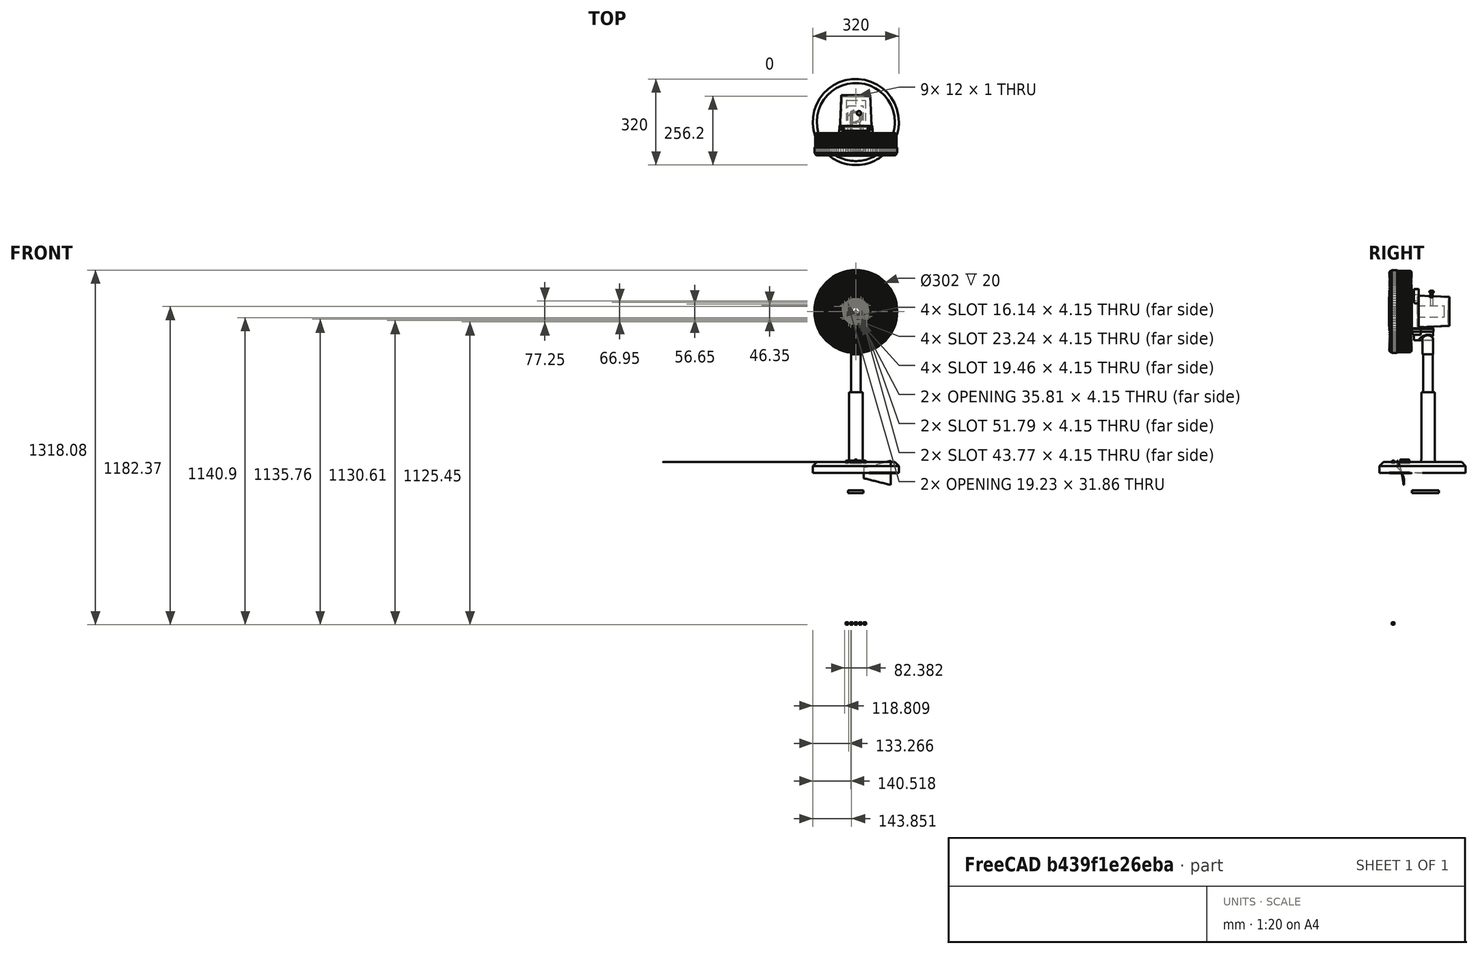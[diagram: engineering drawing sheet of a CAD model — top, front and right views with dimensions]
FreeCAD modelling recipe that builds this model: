
FCSTD DOCUMENT  (FreeCAD 1.0R39109 (Git))
Label: fan
License: All rights reserved
LicenseURL: https://en.wikipedia.org/wiki/All_rights_reserved
objects: Sketcher::SketchObject×53, PartDesign::Pad×37, Part::FeaturePython×22, PartDesign::ShapeBinder×20, PartDesign::Fillet×19, PartDesign::Plane×15, PartDesign::Body×13, App::Part×11, PartDesign::Pocket×9, PartDesign::Line×6, Part::Extrusion×4, PartDesign::Boolean×4, PartDesign::Chamfer×2, Surface::GeomFillSurface×1, Part::Part2DObjectPython×1, Part::Sweep×1
note: 394 computed .brp shape members not serialized (recipe doc carries the construction recipe); baked Part::Feature solids carry a one-line shape summary decoded from their .brp

FEATURE [Sketcher::SketchObject] Sketch
  ArcFitTolerance = 1e-06
  AttachmentSupport = -> [XZ_Plane]
  FullyConstrained = true
  MakeInternals = false
  MapMode = 5
  Placement = pos=(0,0,0) rot=(1,0,0;1.5708rad)
  sketch-geometry (2):
    g0: Circle CenterX=0 CenterY=0 CenterZ=0 NormalX=0 NormalY=0 NormalZ=1 AngleXU=0 Radius=25
    g1: Circle CenterX=0 CenterY=0 CenterZ=0 NormalX=0 NormalY=0 NormalZ=1 AngleXU=0 Radius=40
  constraints (4):
    c: Coincident(g0,g-1)
    c: Coincident(g1,g0)
    c: Radius(g0) = 25
    c: Radius(g1) = 40
FEATURE [PartDesign::Pad] Pad
  Direction = (0,-1,2e-16)
  Length = 30
  Length2 = 10
  Midplane = true
  Placement = pos=(0,0,0) rot=(1,0,0;1.5708rad)
  Profile = -> Sketch
  ReferenceAxis = -> Sketch [N_Axis]
  Refine = true
  Suppressed = false
  Type = 0
FEATURE [PartDesign::ShapeBinder] CopyFace
  Placement = pos=(70,0,0) rot=(0,0,1;0rad)
  TraceSupport = false
FEATURE [PartDesign::Plane] DatumPlane
  AttachmentSupport = -> [CopyFace]
  Length = 94.5083
  MapMode = 5
  Placement = pos=(70,0,0) rot=(0.57735,0.57735,0.57735;2.0944rad)
  ResizeMode = 0
  Width = 297.175
FEATURE [PartDesign::ShapeBinder] CopyFace001
  Placement = pos=(170,0,0) rot=(0,0,1;0rad)
  TraceSupport = false
FEATURE [PartDesign::Plane] DatumPlane001
  AttachmentSupport = -> [CopyFace001]
  Length = 94.5083
  MapMode = 5
  Placement = pos=(170,0,0) rot=(0.57735,0.57735,0.57735;2.0944rad)
  ResizeMode = 0
  Width = 297.175
FEATURE [Sketcher::SketchObject] Sketch002
  ArcFitTolerance = 1e-06
  AttachmentSupport = -> [DatumPlane001]
  FullyConstrained = false
  MakeInternals = false
  MapMode = 5
  Placement = pos=(170,0,0) rot=(0.57735,0.57735,0.57735;2.0944rad)
  sketch-geometry (6):
    g0: Circle [constr] CenterX=-11.7502 CenterY=45 CenterZ=0 NormalX=0 NormalY=0 NormalZ=1 AngleXU=0 Radius=1
    g1: Circle [constr] CenterX=4.45153 CenterY=12.5384 CenterZ=0 NormalX=0 NormalY=0 NormalZ=1 AngleXU=0 Radius=1
    g2: Circle [constr] CenterX=11.7502 CenterY=-45 CenterZ=0 NormalX=0 NormalY=0 NormalZ=1 AngleXU=0 Radius=1
    g3: BSplineCurve PolesCount=3 KnotsCount=2 Degree=2 IsPeriodic=0
    g4: GeomPoint [constr] X=-11.7502 Y=45 Z=0
    g5: GeomPoint [constr] X=11.7502 Y=-45 Z=0
  constraints (10):
    c: Weight(g0) = 1
    c: Equal(g0,g1)
    c: Equal(g0,g2)
    c: InternalAlignment(g0,g3)
    c: InternalAlignment(g1,g3)
    c: InternalAlignment(g2,g3)
    c: InternalAlignment(g4,g3)
    c: InternalAlignment(g5,g3)
    c: Symmetric(g3,g3,g-1)
    c: DistanceY(g3) = 45
FEATURE [Sketcher::SketchObject] Sketch001
  ArcFitTolerance = 1e-06
  AttachmentSupport = -> [DatumPlane]
  ExternalGeometry = -> [Sketch002]
  FullyConstrained = false
  MakeInternals = false
  MapMode = 5
  Placement = pos=(70,0,0) rot=(0.57735,0.57735,0.57735;2.0944rad)
  sketch-geometry (6):
    g0: Circle [constr] CenterX=-11.7502 CenterY=20 CenterZ=0 NormalX=0 NormalY=0 NormalZ=1 AngleXU=0 Radius=1
    g1: Circle [constr] CenterX=3.87626 CenterY=6.1367 CenterZ=0 NormalX=0 NormalY=0 NormalZ=1 AngleXU=0 Radius=1
    g2: Circle [constr] CenterX=11.7502 CenterY=-20 CenterZ=0 NormalX=0 NormalY=0 NormalZ=1 AngleXU=0 Radius=1
    g3: BSplineCurve PolesCount=3 KnotsCount=2 Degree=2 IsPeriodic=0
    g4: GeomPoint [constr] X=-11.7502 Y=20 Z=0
    g5: GeomPoint [constr] X=11.7502 Y=-20 Z=0
  constraints (11):
    c: Weight(g0) = 1
    c: Equal(g0,g1)
    c: Equal(g0,g2)
    c: InternalAlignment(g0,g3)
    c: InternalAlignment(g1,g3)
    c: InternalAlignment(g2,g3)
    c: InternalAlignment(g4,g3)
    c: InternalAlignment(g5,g3)
    c: DistanceY(g3,g3) = 40
    c: Symmetric(g3,g3,g-1)
    c: Vertical(g-3,g3)
FEATURE [Surface::GeomFillSurface] Surface
  BoundaryList = -> [Sketch001,Sketch002]
  FillType = 0
FEATURE [Part::Extrusion] Extrude001
  Base = -> Surface
  Dir = (0,1,0)
  DirMode = 0
  FaceMakerClass = Part::FaceMakerBullseye
  FaceMakerMode = 3
  LengthFwd = 1
  LengthRev = 0
  Placement = pos=(-40,0,0) rot=(0,0,1;0rad)
  Solid = true
  Symmetric = false
FEATURE [Sketcher::SketchObject] Sketch003
  ArcFitTolerance = 1e-06
  AttachmentSupport = -> [XZ_Plane]
  FullyConstrained = true
  MakeInternals = false
  MapMode = 5
  Placement = pos=(0,0,0) rot=(1,0,0;1.5708rad)
FEATURE [Sketcher::SketchObject] Sketch004
  ArcFitTolerance = 1e-06
  AttachmentSupport = -> [XZ_Plane]
  FullyConstrained = false
  MakeInternals = false
  MapMode = 5
  Placement = pos=(0,0,0) rot=(1,0,0;1.5708rad)
  sketch-geometry (6):
    g0: LineSegment StartX=-63.2233 StartY=0.5 StartZ=0 EndX=-63.2233 EndY=-0.5 EndZ=0
    g1: LineSegment StartX=-63.2233 StartY=-0.5 StartZ=0 EndX=-21.9541 EndY=-0.5 EndZ=0
    g2: LineSegment StartX=-21.9541 StartY=-0.5 StartZ=0 EndX=-21.9541 EndY=0.5 EndZ=0
    g3: LineSegment StartX=-21.9541 StartY=0.5 StartZ=0 EndX=-63.2233 EndY=0.5 EndZ=0
    g4: GeomPoint [constr] X=-42.5887 Y=1e-16 Z=0
    g5: Circle CenterX=0 CenterY=0 CenterZ=0 NormalX=0 NormalY=0 NormalZ=1 AngleXU=0 Radius=40
  constraints (12):
    c: Coincident(g0,g1)
    c: Coincident(g1,g2)
    c: Coincident(g2,g3)
    c: Coincident(g3,g0)
    c: Vertical(g0)
    c: Horizontal(g1)
    c: Horizontal(g3)
    c: Symmetric(g2,g0,g4)
    c: DistanceY(g2,g2) = 1
    c: Symmetric(g2,g1,g-1)
    c: Diameter(g5) = 80
    c: Coincident(g5,g-1)
FEATURE [Part::FeaturePython] Array  # Draft array (typed FeaturePython)
  AlwaysSyncPlacement = false
  Angle = 360
  ArrayType = 1
  Axis = (0,1,0)
  Base = -> Extrude001
  Center = (0,0,0)
  Count = 6
  ExpandArray = false
  Fuse = false
  IntervalAxis = (0,0,0)
  IntervalX = (50,0,0)
  IntervalY = (0,50,0)
  IntervalZ = (0,0,50)
  NumberCircles = 3
  NumberPolar = 6
  NumberX = 2
  NumberY = 2
  NumberZ = 1
  PlacementList = 6 placements: [(-40,0,0),(-20,0,34.641),(20,0,34.641),(40,0,4.89859e-15),(20,0,-34.641),(-20,0,-34.641)]
  RadialDistance = 50
  ScaleList = (6) [(1,1,1),(1,1,1),(1,1,1),(1,1,1),(1,1,1),(1,1,1)]
  Symmetry = 1
  TangentialDistance = 25
FEATURE [PartDesign::Boolean] Boolean
  BaseFeature = -> Pad
  Group = -> [Array]
  Refine = true
  Suppressed = false
  Type = 0
  UsePlacement = true
FEATURE [Sketcher::SketchObject] Sketch005
  ArcFitTolerance = 1e-06
  AttachmentSupport = -> [XZ_Plane]
  FullyConstrained = false
  MakeInternals = false
  MapMode = 5
  Placement = pos=(0,0,0) rot=(1,0,0;1.5708rad)
  sketch-geometry (6):
    g0: LineSegment StartX=5.87739 StartY=0.5 StartZ=0 EndX=5.87739 EndY=-0.5 EndZ=0
    g1: LineSegment StartX=5.87739 StartY=-0.5 StartZ=0 EndX=25.7123 EndY=-0.5 EndZ=0
    g2: LineSegment StartX=25.7123 StartY=-0.5 StartZ=0 EndX=25.7123 EndY=0.5 EndZ=0
    g3: LineSegment StartX=25.7123 StartY=0.5 StartZ=0 EndX=5.87739 EndY=0.5 EndZ=0
    g4: GeomPoint [constr] X=15.7948 Y=1e-16 Z=0
    g5: Circle [constr] CenterX=0 CenterY=0 CenterZ=0 NormalX=0 NormalY=0 NormalZ=1 AngleXU=0 Radius=15
  constraints (12):
    c: Coincident(g0,g1)
    c: Coincident(g1,g2)
    c: Coincident(g2,g3)
    c: Coincident(g3,g0)
    c: Vertical(g2)
    c: Horizontal(g1)
    c: Horizontal(g3)
    c: Symmetric(g2,g0,g4)
    c: Diameter(g5) = 30
    c: Coincident(g5,g-1)
    c: Symmetric(g0,g0,g-1)
    c: DistanceY(g0,g0) = 1
FEATURE [Part::Extrusion] Extrude
  Base = -> Sketch005
  Dir = (0,-1,2e-16)
  DirMode = 2
  FaceMakerClass = Part::FaceMakerBullseye
  FaceMakerMode = 3
  LengthFwd = 25
  LengthRev = 0
  Solid = true
  Symmetric = true
FEATURE [Part::FeaturePython] Array001  # Draft array (typed FeaturePython)
  AlwaysSyncPlacement = false
  Angle = 360
  ArrayType = 1
  Axis = (0,1,0)
  Base = -> Extrude
  Center = (0,0,0)
  Count = 6
  ExpandArray = false
  Fuse = false
  IntervalAxis = (0,0,0)
  IntervalX = (50,0,0)
  IntervalY = (0,50,0)
  IntervalZ = (0,0,50)
  NumberCircles = 3
  NumberPolar = 6
  NumberX = 2
  NumberY = 2
  NumberZ = 1
  PlacementList = 6 placements: [(0,0,0),(0,0,0),(0,0,0),(0,0,0),(0,0,0),(0,0,0)]
  RadialDistance = 50
  ScaleList = (6) [(1,1,1),(1,1,1),(1,1,1),(1,1,1),(1,1,1),(1,1,1)]
  Symmetry = 1
  TangentialDistance = 25
FEATURE [PartDesign::Boolean] Boolean001
  BaseFeature = -> Boolean
  Group = -> [Array001]
  Refine = true
  Suppressed = false
  Type = 0
  UsePlacement = true
FEATURE [Sketcher::SketchObject] Sketch006
  ArcFitTolerance = 1e-06
  AttachmentSupport = -> [XZ_Plane]
  FullyConstrained = true
  MakeInternals = false
  MapMode = 5
  Placement = pos=(0,0,0) rot=(1,0,0;1.5708rad)
  sketch-geometry (1):
    g0: Circle CenterX=0 CenterY=0 CenterZ=0 NormalX=0 NormalY=0 NormalZ=1 AngleXU=0 Radius=15
  constraints (2):
    c: Diameter(g0) = 30
    c: Coincident(g0,g-1)
FEATURE [PartDesign::Pad] Pad001
  BaseFeature = -> Boolean001
  Direction = (0,-1,2e-16)
  Length = 30
  Length2 = 10
  Midplane = true
  Profile = -> Sketch006
  ReferenceAxis = -> Sketch006 [N_Axis]
  Refine = true
  Suppressed = false
  Type = 0
FEATURE [Sketcher::SketchObject] Sketch007
  ArcFitTolerance = 1e-06
  AttachmentSupport = -> [Pad001]
  FullyConstrained = true
  MakeInternals = false
  MapMode = 5
  Placement = pos=(0,-12.5,0) rot=(1,0,0;1.5708rad)
  sketch-geometry (1):
    g0: Circle CenterX=0 CenterY=0 CenterZ=0 NormalX=0 NormalY=0 NormalZ=1 AngleXU=0 Radius=25
  constraints (2):
    c: Coincident(g0,g-1)
    c: Radius(g0) = 25
FEATURE [PartDesign::Pad] Pad002
  BaseFeature = -> Pad001
  Direction = (0,-1,2e-16)
  Length = 5
  Length2 = 10
  Profile = -> Sketch007
  ReferenceAxis = -> Sketch007 [N_Axis]
  Refine = true
  Reversed = true
  Suppressed = false
  Type = 0
FEATURE [PartDesign::Chamfer] Chamfer
  Angle = 45
  Base = -> Pad002 [Edge116]
  BaseFeature = -> Pad002
  ChamferType = 0
  FlipDirection = false
  Refine = true
  Size = 2.3
  Size2 = 1
  SupportTransform = false
  Suppressed = false
  UseAllEdges = false
FEATURE [Sketcher::SketchObject] Sketch008
  ArcFitTolerance = 1e-06
  AttachmentSupport = -> [Chamfer]
  FullyConstrained = true
  MakeInternals = false
  MapMode = 5
  Placement = pos=(0,-12.5,2.9e-15) rot=(1,0,0;1.5708rad)
  sketch-geometry (1):
    g0: Circle CenterX=0 CenterY=0 CenterZ=0 NormalX=0 NormalY=0 NormalZ=1 AngleXU=0 Radius=17.5
  constraints (2):
    c: Diameter(g0) = 35
    c: Coincident(g0,g-1)
FEATURE [PartDesign::Pad] Pad003
  BaseFeature = -> Chamfer
  Direction = (0,-1,2e-16)
  Length = 10
  Length2 = 10
  Profile = -> Sketch008
  ReferenceAxis = -> Sketch008 [N_Axis]
  Refine = true
  Suppressed = false
  Type = 0
FEATURE [PartDesign::Plane] DatumPlane002
  AttachmentOffset = pos=(0,0,20) rot=(0,0,1;0rad)
  AttachmentSupport = -> [Pad003]
  Length = 313.007
  MapMode = 5
  Placement = pos=(0,-42.5,9.6e-15) rot=(1,0,0;1.5708rad)
  ResizeMode = 0
  Width = 323.174
FEATURE [PartDesign::Plane] CopyDatumPlane002
  Length = 362.396
  Placement = pos=(0,-42.5,9.7e-15) rot=(1,0,0;1.5708rad)
  ResizeMode = 0
  Width = 362.396
FEATURE [Sketcher::SketchObject] Sketch009
  ArcFitTolerance = 1e-06
  AttachmentSupport = -> [CopyDatumPlane002]
  FullyConstrained = true
  MakeInternals = false
  MapMode = 5
  Placement = pos=(0,-42.5,9.7e-15) rot=(1,0,0;1.5708rad)
  sketch-geometry (1):
    g0: Circle CenterX=0 CenterY=0 CenterZ=0 NormalX=0 NormalY=0 NormalZ=1 AngleXU=0 Radius=55
  constraints (2):
    c: Diameter(g0) = 110
    c: Coincident(g0,g-1)
FEATURE [PartDesign::Pad] Pad004
  Direction = (0,-1,2e-16)
  Length = 5
  Length2 = 10
  Placement = pos=(0,-42.5,9.7e-15) rot=(1,0,0;1.5708rad)
  Profile = -> Sketch009
  ReferenceAxis = -> Sketch009 [N_Axis]
  Refine = true
  Reversed = true
  Suppressed = false
  Type = 0
FEATURE [Sketcher::SketchObject] Sketch011
  ArcFitTolerance = 1e-06
  FullyConstrained = false
  MakeInternals = false
  Placement = pos=(0,0,9.1e-15) rot=(0,0,1;0rad)
  sketch-geometry (5):
    g0: LineSegment StartX=145 StartY=40 StartZ=0 EndX=50 EndY=40 EndZ=0
    g1: LineSegment StartX=145 StartY=-40 StartZ=0 EndX=50 EndY=-40 EndZ=0
    g2: LineSegment StartX=150 StartY=-35 StartZ=0 EndX=150 EndY=35 EndZ=0
    g3: ArcOfCircle CenterX=145 CenterY=35 CenterZ=0 NormalX=0 NormalY=0 NormalZ=1 AngleXU=0 Radius=5 StartAngle=3e-16 EndAngle=1.5708
    g4: ArcOfCircle CenterX=145 CenterY=-35 CenterZ=0 NormalX=0 NormalY=0 NormalZ=1 AngleXU=0 Radius=5 StartAngle=4.71239 EndAngle=6.28319
  constraints (13):
    c: Horizontal(g0)
    c: Horizontal(g1)
    c: Vertical(g2)
    c: Tangent(g0,g3) = -1.5708
    c: Tangent(g2,g3) = -1.5708
    c: Tangent(g2,g4) = -1.5708
    c: Tangent(g1,g4) = 1.5708
    c: DistanceY(g1,g0) = 80
    c: DistanceY(g0) = 40
    c: DistanceX(g1) = 50
    c: DistanceX(g2) = 150
    c: Equal(g3,g4)
    c: Radius(g4) = 5
FEATURE [Part::Part2DObjectPython] Circle  # Draft 2D object (typed FeaturePython)
  Area = 3.14159
  FirstAngle = 0
  LastAngle = 0
  MakeFace = true
  Placement = pos=(50,-40,9.1e-15) rot=(0.57735,0.57735,0.57735;2.0944rad)
  Radius = 1
FEATURE [Part::Sweep] Sweep
  Frenet = true
  Sections = -> [Circle]
  Solid = true
  Spine = -> Sketch011 [Edge1,Edge2,Edge3,Edge4,Edge5]
  Transition = 1
FEATURE [Sketcher::SketchObject] Sketch012
  ArcFitTolerance = 1e-06
  AttachmentSupport = -> [Pad003]
  FullyConstrained = true
  MakeInternals = false
  MapMode = 5
  Placement = pos=(0,15,0) rot=(0,0.707107,0.707107;3.14159rad)
  sketch-geometry (1):
    g0: Circle CenterX=0 CenterY=0 CenterZ=0 NormalX=0 NormalY=0 NormalZ=1 AngleXU=0 Radius=2.5
  constraints (2):
    c: Diameter(g0) = 5
    c: Coincident(g0,g-1)
FEATURE [PartDesign::ShapeBinder] CopyPad005
  Placement = pos=(0,25,-5.6e-15) rot=(0,0,1;0rad)
  TraceSupport = false
FEATURE [Sketcher::SketchObject] Sketch013
  ArcFitTolerance = 1e-06
  AttachmentSupport = -> [CopyPad005]
  FullyConstrained = false
  MakeInternals = false
  MapMode = 5
  Placement = pos=(0,40,-5.6e-15) rot=(0,0.707107,0.707107;3.14159rad)
  sketch-geometry (30):
    g0: ArcOfCircle CenterX=0 CenterY=0 CenterZ=0 NormalX=0 NormalY=0 NormalZ=1 AngleXU=0 Radius=55 StartAngle=6.28319 EndAngle=7.85398
    g1: ArcOfCircle CenterX=0 CenterY=0 CenterZ=0 NormalX=0 NormalY=0 NormalZ=1 AngleXU=0 Radius=49.6 StartAngle=0.107844 EndAngle=0.711077
    g2: ArcOfCircle CenterX=0 CenterY=0 CenterZ=0 NormalX=0 NormalY=0 NormalZ=1 AngleXU=0 Radius=25 StartAngle=2.8576e-06 EndAngle=1.5708
    g3: LineSegment StartX=3.85478 StartY=44.0604 StartZ=0 EndX=4.23487 EndY=48.4048 EndZ=0
    g4: ArcOfCircle CenterX=0 CenterY=0 CenterZ=0 NormalX=0 NormalY=0 NormalZ=1 AngleXU=0 Radius=49.6 StartAngle=0.912359 EndAngle=1.46295
    g5: ArcOfCircle CenterX=0 CenterY=0 CenterZ=0 NormalX=0 NormalY=0 NormalZ=1 AngleXU=0 Radius=43.24 StartAngle=0.917739 EndAngle=1.46092
    g6: ArcOfCircle CenterX=0 CenterY=0 CenterZ=0 NormalX=0 NormalY=0 NormalZ=1 AngleXU=0 Radius=43.24 StartAngle=0.109872 EndAngle=0.691605
    g7: ArcOfCircle CenterX=0 CenterY=0 CenterZ=0 NormalX=0 NormalY=0 NormalZ=1 AngleXU=0 Radius=37.84 StartAngle=0.114414 EndAngle=1.45638
    g8: ArcOfCircle CenterX=0 CenterY=0 CenterZ=0 NormalX=0 NormalY=0 NormalZ=1 AngleXU=0 Radius=31.49 StartAngle=0.11805 EndAngle=1.45275
    g9: LineSegment StartX=27.6374 StartY=34.4826 StartZ=0 EndX=30.4939 EndY=37.786 EndZ=0
    g10: LineSegment StartX=3.20963 StartY=36.6863 StartZ=0 EndX=2.83035 EndY=32.351 EndZ=0
    g11: LineSegment StartX=32.351 StartY=2.83035 StartZ=0 EndX=36.6863 EndY=3.20963 EndZ=0
    g12: LineSegment StartX=33.2878 StartY=28.8322 StartZ=0 EndX=36.0353 EndY=32.3359 EndZ=0
    g13: LineSegment StartX=44.0604 StartY=3.85478 StartZ=0 EndX=48.4048 EndY=4.23487 EndZ=0
    g14: ArcOfCircle CenterX=5.23107 CenterY=48.3177 CenterZ=0 NormalX=0 NormalY=0 NormalZ=1 AngleXU=0 Radius=1 StartAngle=1.46295 EndAngle=3.05433
    g15: ArcOfCircle CenterX=29.7375 CenterY=38.4401 CenterZ=0 NormalX=0 NormalY=0 NormalZ=1 AngleXU=0 Radius=1 StartAngle=5.57022 EndAngle=7.19554
    g16: ArcOfCircle CenterX=36.8222 CenterY=31.7188 CenterZ=0 NormalX=0 NormalY=0 NormalZ=1 AngleXU=0 Radius=1 StartAngle=0.711077 EndAngle=2.47656
    g17: ArcOfCircle CenterX=4.20583 CenterY=36.5991 CenterZ=0 NormalX=0 NormalY=0 NormalZ=1 AngleXU=0 Radius=1 StartAngle=1.45638 EndAngle=3.05433
    g18: ArcOfCircle CenterX=3.82654 CenterY=32.2639 CenterZ=0 NormalX=0 NormalY=0 NormalZ=1 AngleXU=0 Radius=1 StartAngle=3.05433 EndAngle=4.59434
    g19: ArcOfCircle CenterX=4.85098 CenterY=43.9732 CenterZ=0 NormalX=0 NormalY=0 NormalZ=1 AngleXU=0 Radius=1 StartAngle=3.05433 EndAngle=4.60252
    g20: ArcOfCircle CenterX=32.2639 CenterY=3.82654 CenterZ=0 NormalX=0 NormalY=0 NormalZ=1 AngleXU=0 Radius=1 StartAngle=3.25964 EndAngle=4.79966
    g21: ArcOfCircle CenterX=34.0747 CenterY=28.2151 CenterZ=0 NormalX=0 NormalY=0 NormalZ=1 AngleXU=0 Radius=1 StartAngle=2.47656 EndAngle=3.8332
    g22: ArcOfCircle CenterX=36.5991 CenterY=4.20583 CenterZ=0 NormalX=0 NormalY=0 NormalZ=1 AngleXU=0 Radius=1 StartAngle=4.79964 EndAngle=6.3976
    g23: ArcOfCircle CenterX=43.9732 CenterY=4.85098 CenterZ=0 NormalX=0 NormalY=0 NormalZ=1 AngleXU=0 Radius=1 StartAngle=3.25147 EndAngle=4.79966
    g24: ArcOfCircle CenterX=48.3177 CenterY=5.23107 CenterZ=0 NormalX=0 NormalY=0 NormalZ=1 AngleXU=0 Radius=1 StartAngle=4.79966 EndAngle=6.39103
    g25: ArcOfCircle CenterX=26.881 CenterY=35.1367 CenterZ=0 NormalX=0 NormalY=0 NormalZ=1 AngleXU=0 Radius=1 StartAngle=4.05933 EndAngle=5.57022
    g26: LineSegment StartX=25 StartY=7.144e-05 StartZ=0 EndX=55 EndY=-1.05423e-06 EndZ=0
    g27: LineSegment StartX=-9.21207e-05 StartY=55 StartZ=0 EndX=-9.21207e-05 EndY=25 EndZ=0
    g28: LineSegment [constr] StartX=0 StartY=0 StartZ=0 EndX=76.7679 EndY=6.71632 EndZ=0
    g29: LineSegment [constr] StartX=0 StartY=0 StartZ=0 EndX=4.98246 EndY=56.9498 EndZ=0
  constraints (70):
    c: Diameter(g0) = 110
    c: Diameter(g2) = 50
    c: Tangent(g3,g14) = 1.5708
    c: Tangent(g4,g14) = -1.5708
    c: Tangent(g4,g15) = -1.5708
    c: Tangent(g9,g15) = -1.5708
    c: Tangent(g12,g16) = 1.5708
    c: Tangent(g1,g16) = -1.5708
    c: Tangent(g7,g17) = -1.5708
    c: Tangent(g10,g17) = -1.5708
    c: Tangent(g10,g18) = -1.5708
    c: Tangent(g8,g18) = 1.5708
    c: Tangent(g3,g19) = 1.5708
    c: Tangent(g5,g19) = 1.5708
    c: Tangent(g8,g20) = 1.5708
    c: Tangent(g11,g20) = -1.5708
    c: Tangent(g12,g21) = 1.5708
    c: Tangent(g6,g21) = 1.5708
    c: Tangent(g7,g22) = -1.5708
    c: Tangent(g6,g23) = 1.5708
    c: Tangent(g13,g23) = -1.5708
    c: Tangent(g13,g24) = -1.5708
    c: Tangent(g1,g24) = -1.5708
    c: Tangent(g9,g25) = -1.5708
    c: Tangent(g5,g25) = 1.5708
    c: Coincident(g0,g1)
    c: Coincident(g0,g2)
    c: Coincident(g0,g4)
    c: Coincident(g0,g5)
    c: Coincident(g0,g6)
    c: Coincident(g0,g7)
    c: Coincident(g0,g8)
    c: Coincident(g0,g-1)
    c: Radius(g8) = 31.49
    c: Coincident(g26,g0)
    c: Coincident(g26,g2)
    c: Coincident(g27,g0)
    c: Coincident(g27,g2)
    c: Vertical(g27)
    c: Angle(g-1,g28) = 0.0872665
    c: Coincident(g28,g0)
    c: Tangent(g28,g22)
    c: Coincident(g29,g0)
    c: Angle(g29,g-2) = 0.0872665
    c: Radius(g7) = 37.84
    c: Radius(g6) = 43.24
    c: Radius(g1) = 49.6
    c: Radius(g5) = 43.24
    c: Radius(g4) = 49.6
    c: PointOnObject(g10,g29)
    c: PointOnObject(g10,g29)
    c: PointOnObject(g3,g29)
    c: PointOnObject(g3,g29)
    c: PointOnObject(g13,g28)
    c: PointOnObject(g13,g28)
    c: PointOnObject(g11,g28)
    c: PointOnObject(g11,g28)
    c: Equal(g17,g18)
    c: Equal(g17,g20)
    c: Equal(g17,g22)
    c: Equal(g17,g23)
    c: Equal(g17,g24)
    c: Equal(g17,g16)
    c: Equal(g17,g21)
    c: Equal(g17,g15)
    c: Equal(g17,g25)
    c: Equal(g17,g14)
    c: Equal(g17,g19)
    c: Radius(g17) = 1
    c: Coincident(g22,g11)
FEATURE [PartDesign::Pad] Pad006
  Direction = (0,1,-2e-16)
  Length = 5
  Length2 = 10
  Midplane = true
  Placement = pos=(0,25,-5.6e-15) rot=(0,0,1;0rad)
  Profile = -> Sketch013
  ReferenceAxis = -> Sketch013 [N_Axis]
  Refine = true
  Suppressed = false
  Type = 0
FEATURE [Sketcher::SketchObject] Sketch014
  ArcFitTolerance = 1e-06
  AttachmentSupport = -> [Pad006]
  FullyConstrained = false
  MakeInternals = false
  MapMode = 5
  Placement = pos=(0,37.5,-5.6e-15) rot=(1,0,0;1.5708rad)
  sketch-geometry (23):
    g0: Circle CenterX=-1.805e-13 CenterY=-1.057e-13 CenterZ=0 NormalX=0 NormalY=0 NormalZ=1 AngleXU=0 Radius=15
    g1: ArcOfCircle CenterX=-1.805e-13 CenterY=-1.057e-13 CenterZ=0 NormalX=0 NormalY=0 NormalZ=1 AngleXU=0 Radius=35 StartAngle=2.53435 EndAngle=2.70164
    g2: ArcOfCircle CenterX=35.3365 CenterY=61.2046 CenterZ=0 NormalX=0 NormalY=0 NormalZ=1 AngleXU=0 Radius=41.7572 StartAngle=3.82376 EndAngle=4.55382
    g3: ArcOfCircle CenterX=70.673 CenterY=-7.1e-15 CenterZ=0 NormalX=0 NormalY=0 NormalZ=1 AngleXU=0 Radius=41.7572 StartAngle=2.77656 EndAngle=3.50662
    g4: ArcOfCircle CenterX=35.3365 CenterY=-61.2046 CenterZ=0 NormalX=0 NormalY=0 NormalZ=1 AngleXU=0 Radius=41.7572 StartAngle=1.72937 EndAngle=2.45943
    g5: ArcOfCircle CenterX=-35.3365 CenterY=-61.2046 CenterZ=0 NormalX=0 NormalY=0 NormalZ=1 AngleXU=0 Radius=41.7572 StartAngle=0.682168 EndAngle=1.41223
    g6: ArcOfCircle CenterX=-70.673 CenterY=-7.1e-15 CenterZ=0 NormalX=0 NormalY=0 NormalZ=1 AngleXU=0 Radius=41.7572 StartAngle=5.91816 EndAngle=6.64822
    g7: ArcOfCircle CenterX=-35.3365 CenterY=61.2046 CenterZ=0 NormalX=0 NormalY=0 NormalZ=1 AngleXU=0 Radius=41.7572 StartAngle=4.87096 EndAngle=5.60102
    g8: LineSegment [constr] StartX=-31.667 StartY=14.9064 StartZ=0 EndX=-31.667 EndY=-14.9064 EndZ=0
    g9: LineSegment [constr] StartX=31.667 StartY=14.9064 StartZ=0 EndX=31.667 EndY=-14.9064 EndZ=0
    g10: LineSegment [constr] StartX=-35.3365 StartY=61.2046 StartZ=0 EndX=-1.776e-13 EndY=-1.066e-13 EndZ=0
    g11: LineSegment [constr] StartX=35.3365 StartY=61.2046 StartZ=0 EndX=-1.776e-13 EndY=-1.066e-13 EndZ=0
    g12: ArcOfCircle CenterX=-1.805e-13 CenterY=-1.057e-13 CenterZ=0 NormalX=0 NormalY=0 NormalZ=1 AngleXU=0 Radius=35 StartAngle=3.58155 EndAngle=3.74884
    g13: ArcOfCircle CenterX=-1.805e-13 CenterY=-1.057e-13 CenterZ=0 NormalX=0 NormalY=0 NormalZ=1 AngleXU=0 Radius=35 StartAngle=4.62874 EndAngle=4.79604
    g14: ArcOfCircle CenterX=-1.805e-13 CenterY=-1.057e-13 CenterZ=0 NormalX=0 NormalY=0 NormalZ=1 AngleXU=0 Radius=35 StartAngle=5.67594 EndAngle=5.84323
    g15: ArcOfCircle CenterX=-1.805e-13 CenterY=-1.057e-13 CenterZ=0 NormalX=0 NormalY=0 NormalZ=1 AngleXU=0 Radius=35 StartAngle=0.439952 EndAngle=0.607245
    g16: ArcOfCircle CenterX=-1.805e-13 CenterY=-1.057e-13 CenterZ=0 NormalX=0 NormalY=0 NormalZ=1 AngleXU=0 Radius=35 StartAngle=1.48715 EndAngle=1.65444
    g17: LineSegment [constr] StartX=-35.3365 StartY=61.2046 StartZ=0 EndX=-70.673 EndY=-7.1e-15 EndZ=0
    g18: LineSegment [constr] StartX=35.3365 StartY=-61.2046 StartZ=0 EndX=70.673 EndY=-7.1e-15 EndZ=0
    g19: LineSegment [constr] StartX=35.3365 StartY=61.2046 StartZ=0 EndX=70.673 EndY=-7.1e-15 EndZ=0
    g20: LineSegment [constr] StartX=-35.3365 StartY=-61.2046 StartZ=0 EndX=-70.673 EndY=-7.1e-15 EndZ=0
    g21: LineSegment [constr] StartX=-35.3365 StartY=-61.2046 StartZ=0 EndX=35.3365 EndY=-61.2046 EndZ=0
    g22: LineSegment [constr] StartX=-35.3365 StartY=61.2046 StartZ=0 EndX=35.3365 EndY=61.2046 EndZ=0
  constraints (64):
    c: Diameter(g0) = 30
    c: Diameter(g1) = 70
    c: Coincident(g1,g0)
    c: Equal(g7,g2)
    c: Equal(g2,g3)
    c: Equal(g3,g4)
    c: Equal(g4,g5)
    c: Equal(g5,g6)
    c: Symmetric(g3,g6,g-2)
    c: Symmetric(g7,g4,g0)
    c: Symmetric(g2,g5,g0)
    c: Symmetric(g6,g6,g-1)
    c: Coincident(g8,g6)
    c: Coincident(g8,g6)
    c: Coincident(g9,g3)
    c: Coincident(g9,g3)
    c: Vertical(g9)
    c: Equal(g8,g9)
    c: Coincident(g10,g7)
    c: Coincident(g10,g0)
    c: Angle(g-1,g10) = 2.0944
    c: Coincident(g11,g2)
    c: Coincident(g11,g0)
    c: Angle(g-1,g11) = 1.0472
    c: PointOnObject(g2,g16)
    c: PointOnObject(g4,g14)
    c: Coincident(g16,g7)
    c: Coincident(g1,g7)
    c: Equal(g1,g12)
    c: Coincident(g1,g6)
    c: PointOnObject(g12,g6)
    c: Coincident(g1,g12)
    c: Equal(g12,g13)
    c: Coincident(g12,g5)
    c: PointOnObject(g13,g5)
    c: Coincident(g12,g13)
    c: Equal(g13,g14)
    c: Coincident(g13,g4)
    c: PointOnObject(g14,g4)
    c: Coincident(g13,g14)
    c: Equal(g14,g15)
    c: PointOnObject(g14,g3)
    c: PointOnObject(g15,g3)
    c: Coincident(g14,g15)
    c: Equal(g15,g16)
    c: PointOnObject(g16,g2)
    c: Coincident(g15,g16)
    c: Coincident(g15,g2)
    c: Symmetric(g5,g4,g-2)
    c: Coincident(g17,g7)
    c: Coincident(g17,g6)
    c: Coincident(g18,g4)
    c: Coincident(g18,g3)
    c: Coincident(g19,g2)
    c: Coincident(g19,g3)
    c: Coincident(g20,g5)
    c: Coincident(g20,g6)
    c: Coincident(g21,g5)
    c: Coincident(g21,g4)
    c: Coincident(g22,g7)
    c: Coincident(g22,g2)
    c: Equal(g19,g21)
    c: Equal(g21,g20)
    c: Equal(g20,g17)
FEATURE [PartDesign::Fillet] Fillet
  Base = -> Pad006 [Edge6,Edge7]
  BaseFeature = -> Pad006
  Placement = pos=(0,25,-5.6e-15) rot=(0,0,1;0rad)
  Radius = 2
  Refine = true
  SupportTransform = false
  Suppressed = false
  UseAllEdges = false
FEATURE [PartDesign::Fillet] Fillet001
  Base = -> Fillet [Edge31,Edge23,Edge49,Edge64,Edge34,Edge57]
  BaseFeature = -> Fillet
  Placement = pos=(0,25,-5.6e-15) rot=(0,0,1;0rad)
  Radius = 1.5
  Refine = true
  SupportTransform = false
  Suppressed = false
  UseAllEdges = false
FEATURE [PartDesign::Pad] Pad007
  BaseFeature = -> Fillet001
  Direction = (0,-1,2e-16)
  Length = 10
  Length2 = 10
  Placement = pos=(0,25,-5.6e-15) rot=(0,0,1;0rad)
  Profile = -> Sketch014
  ReferenceAxis = -> Sketch014 [N_Axis]
  Refine = true
  Suppressed = false
  Type = 0
FEATURE [PartDesign::Fillet] Fillet002
  Base = -> Pad007 [Edge33,Edge108,Edge119,Edge57,Edge126,Edge125,Edge124,Edge123,Edge122,Edge120,Edge105,Edge121]
  BaseFeature = -> Pad007
  Placement = pos=(0,25,-5.6e-15) rot=(0,0,1;0rad)
  Radius = 3
  Refine = true
  SupportTransform = false
  Suppressed = false
  UseAllEdges = false
FEATURE [PartDesign::Fillet] Fillet003
  Base = -> Fillet002 [Edge71]
  BaseFeature = -> Fillet002
  Placement = pos=(0,25,-5.6e-15) rot=(0,0,1;0rad)
  Radius = 4
  Refine = true
  SupportTransform = false
  Suppressed = false
  UseAllEdges = false
FEATURE [Part::FeaturePython] Array002  # Draft array (typed FeaturePython)
  AlwaysSyncPlacement = false
  Angle = 360
  ArrayType = 1
  Axis = (0,1,0)
  Base = -> Fillet001
  Center = (0,0,0)
  Count = 4
  ExpandArray = false
  Fuse = false
  IntervalAxis = (0,0,0)
  IntervalX = (50,0,0)
  IntervalY = (0,50,0)
  IntervalZ = (0,0,50)
  NumberCircles = 3
  NumberPolar = 4
  NumberX = 2
  NumberY = 2
  NumberZ = 1
  PlacementList = 4 placements: [(0,25,-5.6e-15),(-5.6e-15,25,0),(-6.85802e-31,25,5.6e-15),(5.6e-15,25,1.24345e-30)]
  RadialDistance = 50
  ScaleList = (4) [(1,1,1),(1,1,1),(1,1,1),(1,1,1)]
  Symmetry = 1
  TangentialDistance = 25
FEATURE [PartDesign::Boolean] Boolean002
  BaseFeature = -> Fillet003
  Group = -> [Array002]
  Refine = true
  Suppressed = false
  Type = 0
  UsePlacement = true
FEATURE [PartDesign::Body] Body002
  AllowCompound = false
  Group = -> [CopyPad005,Sketch013,Pad006,Sketch014,Fillet,Fillet001,Pad007,Fillet002,Fillet003,Boolean002]
  Origin = -> Origin002
  Tip = -> Boolean002
FEATURE [PartDesign::ShapeBinder] CopyBoolean002
  TraceSupport = false
FEATURE [Sketcher::SketchObject] Sketch015
  ArcFitTolerance = 1e-06
  AttachmentSupport = -> [CopyBoolean002]
  FullyConstrained = true
  MakeInternals = false
  MapMode = 5
  Placement = pos=(0,42.5,0) rot=(0,0.707107,0.707107;3.14159rad)
  sketch-geometry (1):
    g0: Circle CenterX=0 CenterY=0 CenterZ=0 NormalX=0 NormalY=0 NormalZ=1 AngleXU=0 Radius=60
  constraints (2):
    c: Diameter(g0) = 120
    c: Coincident(g0,g-1)
FEATURE [PartDesign::Pad] Pad008
  Direction = (0,1,-2e-16)
  Length = 140
  Length2 = 10
  Profile = -> Sketch015
  ReferenceAxis = -> Sketch015 [N_Axis]
  Refine = true
  Suppressed = false
  TaperAngle = -2.5
  Type = 0
FEATURE [Sketcher::SketchObject] Sketch016
  ArcFitTolerance = 1e-06
  AttachmentSupport = -> [Pad008]
  FullyConstrained = true
  MakeInternals = false
  MapMode = 5
  Placement = pos=(0,42.5,-9.4e-15) rot=(1,0,0;1.5708rad)
  sketch-geometry (1):
    g0: Circle CenterX=0 CenterY=0 CenterZ=0 NormalX=0 NormalY=0 NormalZ=1 AngleXU=0 Radius=62.5
  constraints (2):
    c: Diameter(g0) = 125
    c: Coincident(g0,g-1)
FEATURE [PartDesign::Pad] Pad009
  BaseFeature = -> Pad008
  Direction = (0,-1,2e-16)
  Length = 25
  Length2 = 10
  Profile = -> Sketch016
  ReferenceAxis = -> Sketch016 [N_Axis]
  Refine = true
  Reversed = true
  Suppressed = false
  TaperAngle = -2.5
  Type = 0
FEATURE [Sketcher::SketchObject] Sketch017
  ArcFitTolerance = 1e-06
  AttachmentSupport = -> [Pad009]
  ExternalGeometry = -> [Pad009]
  FullyConstrained = false
  MakeInternals = false
  MapMode = 5
  Placement = pos=(0,67.5,-1.49e-14) rot=(0,0.707107,0.707107;3.14159rad)
  sketch-geometry (11):
    g0: LineSegment StartX=-54.0278 StartY=29.189 StartZ=0 EndX=-45.1605 EndY=83.7162 EndZ=0
    g1: LineSegment StartX=54.0278 StartY=29.189 StartZ=0 EndX=45.1605 EndY=83.7162 EndZ=0
    g2: LineSegment StartX=45.1605 StartY=83.7162 StartZ=0 EndX=-45.1605 EndY=83.7162 EndZ=0
    g3: LineSegment StartX=-48.063 StartY=38.2223 StartZ=0 EndX=-41.3863 EndY=79.2787 EndZ=0
    g4: LineSegment StartX=-41.3863 StartY=79.2787 StartZ=0 EndX=41.3863 EndY=79.2787 EndZ=0
    g5: LineSegment StartX=41.3863 StartY=79.2787 StartZ=0 EndX=48.063 EndY=38.2223 EndZ=0
    g6: LineSegment [constr] StartX=-43.3631 StartY=67.1232 StartZ=0 EndX=-47.743 EndY=67.8355 EndZ=0
    g7: LineSegment [constr] StartX=-22.8807 StartY=83.7162 StartZ=0 EndX=-22.8807 EndY=79.2787 EndZ=0
    g8: LineSegment [constr] StartX=44.0692 StartY=62.7813 StartZ=0 EndX=48.4491 EndY=63.4935 EndZ=0
    g9: LineSegment StartX=-48.063 StartY=38.2223 StartZ=0 EndX=-54.0278 EndY=29.189 EndZ=0
    g10: LineSegment StartX=48.063 StartY=38.2223 StartZ=0 EndX=54.0278 EndY=29.189 EndZ=0
  constraints (27):
    c: PointOnObject(g0,g-3)
    c: Coincident(g2,g1)
    c: Coincident(g2,g0)
    c: Symmetric(g0,g1,g-2)
    c: Symmetric(g1,g0,g-2)
    c: PointOnObject(g3,g-3)
    c: Coincident(g4,g3)
    c: Horizontal(g4)
    c: Coincident(g5,g4)
    c: PointOnObject(g5,g-3)
    c: Parallel(g3,g0)
    c: Parallel(g5,g1)
    c: PointOnObject(g6,g3)
    c: PointOnObject(g6,g0)
    c: Perpendicular(g3,g6)
    c: PointOnObject(g7,g2)
    c: PointOnObject(g7,g4)
    c: Vertical(g7)
    c: PointOnObject(g8,g5)
    c: PointOnObject(g8,g1)
    c: Perpendicular(g5,g8)
    c: Equal(g8,g7)
    c: Equal(g7,g6)
    c: Coincident(g9,g3)
    c: Coincident(g9,g0)
    c: Coincident(g10,g5)
    c: Coincident(g10,g1)
FEATURE [PartDesign::Pad] Pad010
  BaseFeature = -> Pad009
  Direction = (0,1,-2e-16)
  Length = 17
  Length2 = 10
  Profile = -> Sketch017
  ReferenceAxis = -> Sketch017 [N_Axis]
  Refine = true
  Reversed = true
  Suppressed = false
  Type = 0
FEATURE [Sketcher::SketchObject] Sketch018
  ArcFitTolerance = 1e-06
  AttachmentSupport = -> [Pad010]
  FullyConstrained = true
  MakeInternals = false
  MapMode = 5
  Placement = pos=(0,182.5,-4.02e-14) rot=(0,0.707107,0.707107;3.14159rad)
  sketch-geometry (1):
    g0: Circle CenterX=0 CenterY=0 CenterZ=0 NormalX=0 NormalY=0 NormalZ=1 AngleXU=0 Radius=51
  constraints (2):
    c: Diameter(g0) = 102
    c: Coincident(g0,g-1)
FEATURE [PartDesign::Pocket] Pocket
  BaseFeature = -> Pad010
  Direction = (0,-1,2e-16)
  Length = 120
  Length2 = 5
  Profile = -> Sketch018
  ReferenceAxis = -> Sketch018 [N_Axis]
  Refine = true
  Suppressed = false
  TaperAngle = 2.5
  Type = 0
FEATURE [Sketcher::SketchObject] Sketch019
  ArcFitTolerance = 1e-06
  AttachmentSupport = -> [Pocket]
  FullyConstrained = false
  MakeInternals = false
  MapMode = 5
  Placement = pos=(0,62.5,-1.38e-14) rot=(0,0.707107,0.707107;3.14159rad)
  sketch-geometry (9):
    g0: LineSegment StartX=-23.9794 StartY=-20.7565 StartZ=0 EndX=23.9794 EndY=-20.7565 EndZ=0
    g1: LineSegment StartX=23.9794 StartY=20.7565 StartZ=0 EndX=-23.9794 EndY=20.7565 EndZ=0
    g2: GeomPoint [constr] X=0 Y=0 Z=0
    g3: ArcOfCircle CenterX=-7.77037 CenterY=-8.5e-15 CenterZ=0 NormalX=0 NormalY=0 NormalZ=1 AngleXU=0 Radius=43.5223 StartAngle=5.95653 EndAngle=6.60984
    g4: ArcOfCircle CenterX=7.77037 CenterY=-2.9e-15 CenterZ=0 NormalX=0 NormalY=0 NormalZ=1 AngleXU=0 Radius=43.5223 StartAngle=2.81494 EndAngle=3.46825
    g5: ArcOfCircle CenterX=-23.9794 CenterY=10.7565 CenterZ=0 NormalX=0 NormalY=0 NormalZ=1 AngleXU=0 Radius=10 StartAngle=1.5708 EndAngle=2.81494
    g6: ArcOfCircle CenterX=-23.9794 CenterY=-10.7565 CenterZ=0 NormalX=0 NormalY=0 NormalZ=1 AngleXU=0 Radius=10 StartAngle=3.46825 EndAngle=4.71239
    g7: ArcOfCircle CenterX=23.9794 CenterY=10.7565 CenterZ=0 NormalX=0 NormalY=0 NormalZ=1 AngleXU=0 Radius=10 StartAngle=0.326653 EndAngle=1.5708
    g8: ArcOfCircle CenterX=23.9794 CenterY=-10.7565 CenterZ=0 NormalX=0 NormalY=0 NormalZ=1 AngleXU=0 Radius=10 StartAngle=4.71239 EndAngle=5.95653
  constraints (18):
    c: Horizontal(g0)
    c: Coincident(g2,g-1)
    c: Equal(g4,g3)
    c: Tangent(g4,g5) = -1.5708
    c: Tangent(g1,g5) = -1.5708
    c: Tangent(g4,g6) = -1.5708
    c: Tangent(g0,g6) = -1.5708
    c: Tangent(g1,g7) = -1.5708
    c: Tangent(g3,g7) = -1.5708
    c: Tangent(g0,g8) = -1.5708
    c: Tangent(g3,g8) = -1.5708
    c: Equal(g8,g7)
    c: Equal(g8,g5)
    c: Equal(g8,g6)
    c: Radius(g8) = 10
    c: Symmetric(g7,g6,g2)
    c: Symmetric(g5,g8,g2)
    c: Vertical(g4,g4)
FEATURE [PartDesign::Pad] Pad011
  BaseFeature = -> Pocket
  Direction = (0,1,-2e-16)
  Length = 100
  Length2 = 10
  Profile = -> Sketch019
  ReferenceAxis = -> Sketch019 [N_Axis]
  Refine = true
  Suppressed = false
  Type = 0
FEATURE [Sketcher::SketchObject] Sketch020
  ArcFitTolerance = 1e-06
  AttachmentSupport = -> [Pad011]
  ExternalGeometry = -> [Pad011]
  FullyConstrained = false
  MakeInternals = false
  MapMode = 5
  Placement = pos=(0,42.5,-1.11e-14) rot=(1,0,0;1.5708rad)
  sketch-geometry (2):
    g0: LineSegment [constr] StartX=0 StartY=-62.5 StartZ=0 EndX=0 EndY=-64.5 EndZ=0
    g1: LineSegment StartX=-28.4155 StartY=-64.5 StartZ=0 EndX=28.4155 EndY=-64.5 EndZ=0
  constraints (5):
    c: PointOnObject(g0,g-3)
    c: Vertical(g0)
    c: DistanceY(g0,g0) = 2
    c: Symmetric(g1,g1,g-2)
    c: Symmetric(g1,g1,g0)
FEATURE [Part::Extrusion] Extrude003
  Base = -> Sketch020
  Dir = (0,1,0)
  DirMode = 0
  FaceMakerClass = Part::FaceMakerBullseye
  FaceMakerMode = 3
  LengthFwd = 100
  LengthRev = 0
  Solid = false
  Symmetric = false
FEATURE [PartDesign::ShapeBinder] CopyPad011
  Placement = pos=(0,42.5,-9.4e-15) rot=(1,0,0;1.5708rad)
  TraceSupport = false
FEATURE [PartDesign::Line] DatumLine
  AttacherType = Attacher::AttachEngineLine
  AttachmentSupport = -> [CopyPad011]
  Length = 20
  MapMode = 19
  Placement = pos=(0,42.5,-9.4e-15) rot=(1,0,0;1.5708rad)
  ResizeMode = 0
FEATURE [Part::Extrusion] Extrude004
  Base = -> Extrude003
  Dir = (0,0,-1)
  DirMode = 2
  FaceMakerClass = Part::FaceMakerBullseye
  FaceMakerMode = 3
  LengthFwd = 10
  LengthRev = 0
  Solid = true
  Symmetric = false
FEATURE [PartDesign::ShapeBinder] CopyExtrude003
  TraceSupport = false
FEATURE [PartDesign::Plane] DatumPlane004
  AttachmentSupport = -> [CopyExtrude003]
  Length = 67.1756
  MapMode = 5
  Placement = pos=(0,0,-64.5) rot=(1,0,0;3.14159rad)
  ResizeMode = 0
  Width = 164.676
FEATURE [Sketcher::SketchObject] Sketch021
  ArcFitTolerance = 1e-06
  AttachmentSupport = -> [DatumPlane004]
  ExternalGeometry = -> [CopyPad011]
  FullyConstrained = false
  MakeInternals = false
  MapMode = 5
  Placement = pos=(0,0,-64.5) rot=(1,0,0;3.14159rad)
  sketch-geometry (12):
    g0: GeomPoint [constr] X=0 Y=-146.096 Z=0
    g1: GeomPoint [constr] X=-20 Y=-122.501 Z=0
    g2: GeomPoint [constr] X=20 Y=-122.501 Z=0
    g3: ArcOfCircle CenterX=0.00115096 CenterY=-65.0006 CenterZ=0 NormalX=0 NormalY=0 NormalZ=1 AngleXU=0 Radius=22.5 StartAngle=5.80719 EndAngle=9.90077
    g4: LineSegment StartX=20 StartY=-117.501 StartZ=0 EndX=20 EndY=-75.3107 EndZ=0
    g5: LineSegment StartX=-19.9977 StartY=-75.3106 StartZ=0 EndX=-19.9998 EndY=-117.5 EndZ=0
    g6: LineSegment StartX=-14.9998 StartY=-122.501 StartZ=0 EndX=15 EndY=-122.501 EndZ=0
    g7: GeomPoint [constr] X=0.00115171 Y=-98.9056 Z=0
    g8: ArcOfCircle CenterX=15 CenterY=-117.501 CenterZ=0 NormalX=0 NormalY=0 NormalZ=1 AngleXU=0 Radius=5 StartAngle=4.71239 EndAngle=6.28319
    g9: GeomPoint [constr] X=20 Y=-122.501 Z=0
    g10: ArcOfCircle CenterX=-14.9998 CenterY=-117.501 CenterZ=0 NormalX=0 NormalY=0 NormalZ=1 AngleXU=0 Radius=5 StartAngle=3.14154 EndAngle=4.71239
    g11: GeomPoint [constr] X=-20 Y=-122.501 Z=0
  constraints (15):
    c: DistanceX(g1,g2) = 40
    c: Radius(g3) = 22.5
    c: Symmetric(g5,g9,g7)
    c: Coincident(g4,g3)
    c: PointOnObject(g9,g6)
    c: PointOnObject(g9,g4)
    c: Tangent(g6,g8) = -1.5708
    c: Tangent(g4,g8) = -1.5708
    c: PointOnObject(g11,g6)
    c: PointOnObject(g11,g5)
    c: Tangent(g6,g10) = -1.5708
    c: Tangent(g5,g10) = -1.5708
    c: Equal(g8,g10)
    c: Radius(g8) = 5
    c: Coincident(g3,g5)
FEATURE [PartDesign::Pad] Pad012
  Direction = (0,0,-1)
  Length = 10
  Length2 = 10
  Placement = pos=(0,0,-64.5) rot=(1,0,0;3.14159rad)
  Profile = -> Sketch021
  ReferenceAxis = -> Sketch021 [N_Axis]
  Refine = true
  Suppressed = false
  Type = 0
FEATURE [Sketcher::SketchObject] Sketch022
  ArcFitTolerance = 1e-06
  AttachmentSupport = -> [Pad012]
  ExternalGeometry = -> [Pad012]
  FullyConstrained = false
  MakeInternals = false
  MapMode = 5
  Placement = pos=(0,0,-74.5) rot=(1,0,0;3.14159rad)
  sketch-geometry (12):
    g0: ArcOfCircle CenterX=0.00115096 CenterY=-65.0006 CenterZ=0 NormalX=0 NormalY=0 NormalZ=1 AngleXU=0 Radius=20.5 StartAngle=5.78404 EndAngle=9.92369
    g1: LineSegment StartX=-18 StartY=-74.8092 StartZ=0 EndX=-18 EndY=-117.5 EndZ=0
    g2: LineSegment StartX=-14.9998 StartY=-120.501 StartZ=0 EndX=15 EndY=-120.501 EndZ=0
    g3: LineSegment StartX=18 StartY=-117.501 StartZ=0 EndX=18 EndY=-74.8135 EndZ=0
    g4: LineSegment [constr] StartX=-20 StartY=-122.501 StartZ=0 EndX=-18 EndY=-122.501 EndZ=0
    g5: LineSegment [constr] StartX=-5.54657 StartY=-120.501 StartZ=0 EndX=-5.54657 EndY=-122.501 EndZ=0
    g6: ArcOfCircle CenterX=-14.9998 CenterY=-117.5 CenterZ=0 NormalX=0 NormalY=0 NormalZ=1 AngleXU=0 Radius=3.00024 StartAngle=3.14159 EndAngle=4.71239
    g7: GeomPoint [constr] X=-18 Y=-120.501 Z=0
    g8: ArcOfCircle CenterX=15 CenterY=-117.501 CenterZ=0 NormalX=0 NormalY=0 NormalZ=1 AngleXU=0 Radius=3 StartAngle=4.71239 EndAngle=6.28319
    g9: GeomPoint [constr] X=18 Y=-120.501 Z=0
    g10: LineSegment [constr] StartX=15 StartY=-120.501 StartZ=0 EndX=15 EndY=-122.501 EndZ=0
    g11: LineSegment [constr] StartX=18 StartY=-117.501 StartZ=0 EndX=20 EndY=-117.501 EndZ=0
  constraints (30):
    c: Diameter(g0) = 41
    c: Coincident(g0,g-3)
    c: Vertical(g1)
    c: Vertical(g3)
    c: PointOnObject(g4,g-4)
    c: PointOnObject(g4,g1)
    c: Horizontal(g4)
    c: DistanceX(g4,g4) = 2
    c: Symmetric(g9,g7,g-2)
    c: PointOnObject(g5,g2)
    c: Vertical(g5)
    c: PointOnObject(g5,g-5)
    c: Equal(g5,g4)
    c: PointOnObject(g7,g1)
    c: PointOnObject(g7,g2)
    c: Tangent(g1,g6) = -1.5708
    c: Tangent(g2,g6) = -1.5708
    c: PointOnObject(g9,g3)
    c: PointOnObject(g9,g2)
    c: Tangent(g3,g8) = -1.5708
    c: Tangent(g2,g8) = -1.5708
    c: Coincident(g10,g2)
    c: Coincident(g10,g-5)
    c: Coincident(g11,g3)
    c: Horizontal(g11)
    c: Coincident(g11,g-6)
    c: Vertical(g10)
    c: Vertical(g2,g-5)
    c: Coincident(g0,g1)
    c: Coincident(g0,g3)
FEATURE [PartDesign::Pad] Pad013
  BaseFeature = -> Pad012
  Direction = (0,0,-1)
  Length = 12
  Length2 = 10
  Placement = pos=(0,0,-64.5) rot=(1,0,0;3.14159rad)
  Profile = -> Sketch022
  ReferenceAxis = -> Sketch022 [N_Axis]
  Refine = true
  Suppressed = false
  Type = 0
FEATURE [Sketcher::SketchObject] Sketch023
  ArcFitTolerance = 1e-06
  AttachmentSupport = -> [Pad013]
  ExternalGeometry = -> [Pad013]
  FullyConstrained = false
  MakeInternals = false
  MapMode = 5
  Placement = pos=(0,0,-86.5) rot=(1,0,0;3.14159rad)
  sketch-geometry (8):
    g0: LineSegment StartX=-18 StartY=-74.81 StartZ=0 EndX=-18 EndY=-117.5 EndZ=0
    g1: LineSegment StartX=-14.9998 StartY=-120.501 StartZ=0 EndX=15 EndY=-120.501 EndZ=0
    g2: LineSegment StartX=18 StartY=-117.501 StartZ=0 EndX=18 EndY=-74.81 EndZ=0
    g3: ArcOfCircle CenterX=-14.9998 CenterY=-117.5 CenterZ=0 NormalX=0 NormalY=0 NormalZ=1 AngleXU=0 Radius=3.00024 StartAngle=3.14159 EndAngle=4.71239
    g4: ArcOfCircle CenterX=15 CenterY=-117.501 CenterZ=0 NormalX=0 NormalY=0 NormalZ=1 AngleXU=0 Radius=3 StartAngle=4.71239 EndAngle=6.28319
    g5: ArcOfCircle CenterX=4e-16 CenterY=-67.5389 CenterZ=0 NormalX=0 NormalY=0 NormalZ=1 AngleXU=0 Radius=18 StartAngle=5e-16 EndAngle=3.14159
    g6: LineSegment StartX=18 StartY=-67.5389 StartZ=0 EndX=18 EndY=-74.81 EndZ=0
    g7: LineSegment StartX=-18 StartY=-67.5389 StartZ=0 EndX=-18 EndY=-74.81 EndZ=0
  constraints (18):
    c: Vertical(g0)
    c: Vertical(g2)
    c: Tangent(g0,g3) = -1.5708
    c: Tangent(g1,g3) = -1.5708
    c: Tangent(g2,g4) = -1.5708
    c: Tangent(g1,g4) = -1.5708
    c: Tangent(g5,g6) = 1.5708
    c: Tangent(g5,g7) = -1.5708
    c: DistanceX(g-1,g2) = 18
    c: DistanceX(g0) = -18
    c: DistanceY(g0) = -74.81
    c: DistanceY(g2) = -74.81
    c: DistanceX(g5,g5) = 36
    c: Coincident(g6,g2)
    c: Coincident(g7,g0)
    c: Vertical(g7)
    c: Coincident(g1,g-7)
    c: Coincident(g1,g-7)
FEATURE [PartDesign::Pad] Pad014
  BaseFeature = -> Pad013
  Direction = (0,0,-1)
  Length = 20
  Length2 = 10
  Placement = pos=(0,0,-64.5) rot=(1,0,0;3.14159rad)
  Profile = -> Sketch023
  ReferenceAxis = -> Sketch023 [N_Axis]
  Refine = true
  Suppressed = false
  Type = 0
FEATURE [Sketcher::SketchObject] Sketch024
  ArcFitTolerance = 1e-06
  AttachmentSupport = -> [Pad014]
  ExternalGeometry = -> [Pad014]
  FullyConstrained = false
  MakeInternals = false
  MapMode = 5
  Placement = pos=(18,0,-64.5) rot=(0.57735,-0.57735,0.57735;4.18879rad)
  sketch-geometry (4):
    g0: LineSegment StartX=-120.501 StartY=42 StartZ=0 EndX=-120.501 EndY=26 EndZ=0
    g1: ArcOfCircle CenterX=-102.813 CenterY=63.1065 CenterZ=0 NormalX=0 NormalY=0 NormalZ=1 AngleXU=0 Radius=41.1065 StartAngle=4.26758 EndAngle=5.74397
    g2: LineSegment [constr] StartX=-74.8135 StartY=22 StartZ=0 EndX=-113.793 EndY=22 EndZ=0
    g3: LineSegment StartX=-120.501 StartY=42 StartZ=0 EndX=-67.5389 EndY=42 EndZ=0
  constraints (9):
    c: Coincident(g0,g-3)
    c: Symmetric(g-3,g-3,g0)
    c: Coincident(g1,g-4)
    c: Coincident(g1,g0)
    c: Coincident(g2,g-5)
    c: Horizontal(g2)
    c: Tangent(g2,g1)
    c: Coincident(g3,g0)
    c: Coincident(g3,g1)
FEATURE [PartDesign::Pocket] Pocket001
  BaseFeature = -> Pad014
  Direction = (-1,0,0)
  Length = 5
  Length2 = 5
  Placement = pos=(0,0,-64.5) rot=(1,0,0;3.14159rad)
  Profile = -> Sketch024
  ReferenceAxis = -> Sketch024 [N_Axis]
  Refine = true
  Suppressed = false
  Type = 0
FEATURE [Sketcher::SketchObject] Sketch025
  ArcFitTolerance = 1e-06
  AttachmentSupport = -> [Pocket001]
  ExternalGeometry = -> [Pocket001]
  FullyConstrained = false
  MakeInternals = false
  MapMode = 5
  Placement = pos=(-18,0,-64.5) rot=(0.57735,0.57735,-0.57735;4.18879rad)
  sketch-geometry (4):
    g0: LineSegment [constr] StartX=74.8135 StartY=22 StartZ=0 EndX=110.463 EndY=22 EndZ=0
    g1: LineSegment StartX=120.501 StartY=42 StartZ=0 EndX=120.501 EndY=26 EndZ=0
    g2: ArcOfCircle CenterX=102.813 CenterY=63.1065 CenterZ=0 NormalX=0 NormalY=0 NormalZ=1 AngleXU=0 Radius=41.1065 StartAngle=3.6808 EndAngle=5.1572
    g3: LineSegment StartX=120.501 StartY=42 StartZ=0 EndX=67.5389 EndY=42 EndZ=0
  constraints (9):
    c: Coincident(g0,g-4)
    c: Horizontal(g0)
    c: Coincident(g1,g-3)
    c: Symmetric(g-3,g-3,g1)
    c: Coincident(g2,g-5)
    c: Coincident(g2,g1)
    c: Tangent(g0,g2)
    c: Coincident(g3,g1)
    c: Coincident(g3,g2)
FEATURE [PartDesign::Pocket] Pocket002
  BaseFeature = -> Pocket001
  Direction = (1,0,0)
  Length = 5
  Length2 = 5
  Placement = pos=(0,0,-64.5) rot=(1,0,0;3.14159rad)
  Profile = -> Sketch025
  ReferenceAxis = -> Sketch025 [N_Axis]
  Refine = true
  Suppressed = false
  Type = 0
FEATURE [Sketcher::SketchObject] Sketch026
  ArcFitTolerance = 1e-06
  AttachmentSupport = -> [Pocket002]
  ExternalGeometry = -> [Pocket002]
  FullyConstrained = true
  MakeInternals = false
  MapMode = 5
  Placement = pos=(0,120.501,-64.5) rot=(-1,0,0;1.5708rad)
  sketch-geometry (4):
    g0: LineSegment StartX=-13 StartY=26 StartZ=0 EndX=13 EndY=26 EndZ=0
    g1: LineSegment StartX=13 StartY=26 StartZ=0 EndX=13 EndY=42 EndZ=0
    g2: LineSegment StartX=13 StartY=42 StartZ=0 EndX=-13 EndY=42 EndZ=0
    g3: LineSegment StartX=-13 StartY=42 StartZ=0 EndX=-13 EndY=26 EndZ=0
  constraints (10):
    c: Coincident(g0,g1)
    c: Coincident(g1,g2)
    c: Coincident(g2,g3)
    c: Coincident(g3,g0)
    c: Horizontal(g0)
    c: Horizontal(g2)
    c: Vertical(g1)
    c: Vertical(g3)
    c: Coincident(g0,g-4)
    c: Coincident(g1,g-3)
FEATURE [PartDesign::Pocket] Pocket003
  BaseFeature = -> Pocket002
  Direction = (0,-1,-2e-16)
  Length = 3
  Length2 = 5
  Placement = pos=(0,0,-64.5) rot=(1,0,0;3.14159rad)
  Profile = -> Sketch026
  ReferenceAxis = -> Sketch026 [N_Axis]
  Refine = true
  Suppressed = false
  Type = 0
FEATURE [Sketcher::SketchObject] Sketch027
  ArcFitTolerance = 1e-06
  AttachmentSupport = -> [Pocket003]
  ExternalGeometry = -> [Pocket003]
  FullyConstrained = false
  MakeInternals = false
  MapMode = 5
  Placement = pos=(13,0,-64.5) rot=(0.57735,-0.57735,0.57735;4.18879rad)
  sketch-geometry (4):
    g0: LineSegment StartX=-82.15 StartY=35.0443 StartZ=0 EndX=-82.15 EndY=95.0443 EndZ=0
    g1: LineSegment StartX=-120.501 StartY=35.0443 StartZ=0 EndX=-120.501 EndY=95.0443 EndZ=0
    g2: ArcOfCircle CenterX=-101.325 CenterY=45.8538 CenterZ=0 NormalX=0 NormalY=0 NormalZ=1 AngleXU=0 Radius=22.0122 StartAngle=3.65491 EndAngle=5.76987
    g3: LineSegment StartX=-82.15 StartY=95.0443 StartZ=0 EndX=-120.501 EndY=95.0443 EndZ=0
  constraints (11):
    c: Distance(g0) = 60
    c: Vertical(g0)
    c: Distance(g1) = 60
    c: Vertical(g1)
    c: Coincident(g2,g1)
    c: Coincident(g2,g0)
    c: Vertical(g-3,g1)
    c: Horizontal(g0,g1)
    c: Coincident(g3,g0)
    c: Coincident(g3,g1)
    c: DistanceX(g0) = -82.15
FEATURE [PartDesign::Pad] Pad015
  BaseFeature = -> Pocket003
  Direction = (1,0,0)
  Length = 5
  Length2 = 10
  Placement = pos=(0,0,-64.5) rot=(1,0,0;3.14159rad)
  Profile = -> Sketch027
  ReferenceAxis = -> Sketch027 [N_Axis]
  Refine = true
  Suppressed = false
  Type = 0
FEATURE [Sketcher::SketchObject] Sketch028
  ArcFitTolerance = 1e-06
  AttachmentSupport = -> [Pad015]
  ExternalGeometry = -> [Pad015]
  FullyConstrained = false
  MakeInternals = false
  MapMode = 5
  Placement = pos=(-13,0,-64.5) rot=(0.57735,0.57735,-0.57735;4.18879rad)
  sketch-geometry (4):
    g0: LineSegment StartX=82.15 StartY=35.0443 StartZ=0 EndX=82.15 EndY=95.0443 EndZ=0
    g1: LineSegment StartX=120.501 StartY=35.0443 StartZ=0 EndX=120.501 EndY=95.0443 EndZ=0
    g2: ArcOfCircle CenterX=101.325 CenterY=45.8538 CenterZ=0 NormalX=0 NormalY=0 NormalZ=1 AngleXU=0 Radius=22.0122 StartAngle=3.65491 EndAngle=5.76987
    g3: LineSegment StartX=82.15 StartY=95.0443 StartZ=0 EndX=120.501 EndY=95.0443 EndZ=0
  constraints (6):
    c: Vertical(g0)
    c: Vertical(g1)
    c: Coincident(g2,g1)
    c: Coincident(g2,g0)
    c: Coincident(g3,g0)
    c: Coincident(g3,g1)
FEATURE [PartDesign::Pad] Pad016
  BaseFeature = -> Pad015
  Direction = (-1,0,0)
  Length = 5
  Length2 = 10
  Placement = pos=(0,0,-64.5) rot=(1,0,0;3.14159rad)
  Profile = -> Sketch028
  ReferenceAxis = -> Sketch028 [N_Axis]
  Refine = true
  Suppressed = false
  Type = 0
FEATURE [Sketcher::SketchObject] Sketch029
  ArcFitTolerance = 1e-06
  AttachmentSupport = -> [Pad016]
  ExternalGeometry = -> [Pad016]
  FullyConstrained = false
  MakeInternals = false
  MapMode = 5
  Placement = pos=(0,120.501,-64.5) rot=(-1,0,0;1.5708rad)
  sketch-geometry (4):
    g0: LineSegment StartX=-13 StartY=38.7552 StartZ=0 EndX=-13 EndY=44 EndZ=0
    g1: LineSegment StartX=-13 StartY=44 StartZ=0 EndX=13 EndY=44 EndZ=0
    g2: LineSegment StartX=13 StartY=44 StartZ=0 EndX=13 EndY=38.7552 EndZ=0
    g3: LineSegment StartX=13 StartY=38.7552 StartZ=0 EndX=-13 EndY=38.7552 EndZ=0
  constraints (11):
    c: Vertical(g0)
    c: DistanceY(g-5,g0) = 2
    c: Vertical(g-5,g0)
    c: Coincident(g1,g0)
    c: Horizontal(g1)
    c: Coincident(g2,g1)
    c: Vertical(g2)
    c: Coincident(g3,g2)
    c: Coincident(g3,g0)
    c: Horizontal(g3)
    c: PointOnObject(g-5,g2)
FEATURE [PartDesign::Pad] Pad017
  BaseFeature = -> Pad016
  Direction = (0,1,2e-16)
  Length = 2
  Length2 = 10
  Placement = pos=(0,0,-64.5) rot=(1,0,0;3.14159rad)
  Profile = -> Sketch029
  ReferenceAxis = -> Sketch029 [N_Axis]
  Refine = true
  Reversed = true
  Suppressed = false
  Type = 0
FEATURE [PartDesign::ShapeBinder] CopyPad020
  Placement = pos=(0,2.33659e-09,-260) rot=(0,0,1;0rad)
  TraceSupport = false
FEATURE [PartDesign::Plane] DatumPlane005
  AttachmentSupport = -> [CopyPad020]
  Length = 383.929
  MapMode = 5
  Placement = pos=(0,5.0286e-09,-559.544) rot=(1,0,0;3.14159rad)
  ResizeMode = 0
  Width = 383.96
FEATURE [PartDesign::ShapeBinder] CopyPad021
  Placement = pos=(0,2.33659e-09,-260) rot=(0,0,1;0rad)
  TraceSupport = false
FEATURE [Sketcher::SketchObject] Sketch034
  ArcFitTolerance = 1e-06
  AttachmentSupport = -> [CopyPad021]
  ExternalGeometry = -> [CopyPad021]
  FullyConstrained = true
  MakeInternals = false
  MapMode = 5
  Placement = pos=(0,5.0286e-09,-559.544) rot=(1,0,0;3.14159rad)
  sketch-geometry (2):
    g0: Circle CenterX=0 CenterY=-82.2978 CenterZ=0 NormalX=0 NormalY=0 NormalZ=1 AngleXU=0 Radius=160
    g1: LineSegment [constr] StartX=0 StartY=-102.298 StartZ=0 EndX=0 EndY=-242.298 EndZ=0
  constraints (6):
    c: Diameter(g0) = 320
    c: PointOnObject(g0,g-2)
    c: Coincident(g1,g-3)
    c: PointOnObject(g1,g0)
    c: Vertical(g1)
    c: DistanceY(g1,g1) = 140
FEATURE [PartDesign::Pad] Pad021
  Direction = (0,8.987e-12,-1)
  Length = 40
  Length2 = 10
  Placement = pos=(0,2.33659e-09,-260) rot=(0,0,1;0rad)
  Profile = -> Sketch034
  ReferenceAxis = -> Sketch034 [N_Axis]
  Refine = true
  Suppressed = false
  Type = 0
FEATURE [Sketcher::SketchObject] Sketch030
  ArcFitTolerance = 1e-06
  AttachmentSupport = -> [Pad017]
  ExternalGeometry = -> [Pad017]
  FullyConstrained = true
  MakeInternals = false
  MapMode = 5
  Placement = pos=(8.98118e-07,120.501,-64.5) rot=(-1,0,0;1.5708rad)
  sketch-geometry (4):
    g0: LineSegment StartX=-13 StartY=95.0443 StartZ=0 EndX=-13 EndY=44 EndZ=0
    g1: LineSegment StartX=-13 StartY=44 StartZ=0 EndX=13 EndY=44 EndZ=0
    g2: LineSegment StartX=13 StartY=44 StartZ=0 EndX=13 EndY=95.0443 EndZ=0
    g3: LineSegment StartX=13 StartY=95.0443 StartZ=0 EndX=-13 EndY=95.0443 EndZ=0
  constraints (10):
    c: Coincident(g0,g1)
    c: Coincident(g1,g2)
    c: Coincident(g2,g3)
    c: Coincident(g3,g0)
    c: Vertical(g0)
    c: Vertical(g2)
    c: Horizontal(g1)
    c: Horizontal(g3)
    c: Coincident(g0,g-3)
    c: Coincident(g1,g-4)
FEATURE [PartDesign::Pad] Pad018
  BaseFeature = -> Pad017
  Direction = (7.45322e-09,1,2.56963e-11)
  Length = 10
  Length2 = 10
  Placement = pos=(0,0,-64.5) rot=(1,0,0;3.14159rad)
  Profile = -> Sketch030
  ReferenceAxis = -> Sketch030 [N_Axis]
  Refine = true
  Reversed = true
  Suppressed = false
  Type = 3
  UpToFace = -> Pad017 [Face27]
FEATURE [Sketcher::SketchObject] Sketch035
  ArcFitTolerance = 1e-06
  AttachmentSupport = -> [Pad021]
  ExternalGeometry = -> [CopyPad020]
  FullyConstrained = true
  MakeInternals = false
  MapMode = 5
  Placement = pos=(7.19e-14,5.02858e-09,-559.544) rot=(0,0,1;0rad)
  sketch-geometry (1):
    g0: Circle CenterX=0 CenterY=102.298 CenterZ=0 NormalX=0 NormalY=0 NormalZ=1 AngleXU=0 Radius=25
  constraints (2):
    c: Coincident(g0,g-3)
    c: Radius(g0) = 25
FEATURE [PartDesign::Pad] Pad022
  BaseFeature = -> Pad021
  Direction = (0,-8.987e-12,1)
  Length = 260
  Length2 = 10
  Placement = pos=(0,2.33659e-09,-260) rot=(0,0,1;0rad)
  Profile = -> Sketch035
  ReferenceAxis = -> Sketch035 [N_Axis]
  Refine = true
  Suppressed = false
  Type = 0
FEATURE [PartDesign::Fillet] Fillet004
  Base = -> Pad022 [Edge4]
  BaseFeature = -> Pad022
  Placement = pos=(0,2.33659e-09,-260) rot=(0,0,1;0rad)
  Radius = 10
  Refine = true
  SupportTransform = false
  Suppressed = false
  UseAllEdges = false
FEATURE [Sketcher::SketchObject] Sketch036
  ArcFitTolerance = 1e-06
  AttachmentSupport = -> [Fillet004]
  FullyConstrained = false
  MakeInternals = false
  MapMode = 5
  Placement = pos=(7.19e-14,5.02858e-09,-559.544) rot=(0,0,1;0rad)
  sketch-geometry (10):
    g0: Circle CenterX=0 CenterY=15.7896 CenterZ=0 NormalX=0 NormalY=0 NormalZ=1 AngleXU=0 Radius=18.5
    g1: Circle CenterX=-32.7753 CenterY=-26.9693 CenterZ=0 NormalX=0 NormalY=0 NormalZ=1 AngleXU=0 Radius=5.5
    g2: Circle CenterX=-16.3876 CenterY=-26.9693 CenterZ=0 NormalX=0 NormalY=0 NormalZ=1 AngleXU=0 Radius=5.5
    g3: Circle CenterX=0 CenterY=-26.9693 CenterZ=0 NormalX=0 NormalY=0 NormalZ=1 AngleXU=0 Radius=5.5
    g4: Circle CenterX=16.3876 CenterY=-26.9693 CenterZ=0 NormalX=0 NormalY=0 NormalZ=1 AngleXU=0 Radius=5.5
    g5: Circle CenterX=32.7753 CenterY=-26.9693 CenterZ=0 NormalX=0 NormalY=0 NormalZ=1 AngleXU=0 Radius=5.5
    g6: LineSegment [constr] StartX=-32.7753 StartY=-26.9693 StartZ=0 EndX=-16.3876 EndY=-26.9693 EndZ=0
    g7: LineSegment [constr] StartX=-16.3876 StartY=-26.9693 StartZ=0 EndX=0 EndY=-26.9693 EndZ=0
    g8: LineSegment [constr] StartX=0 StartY=-26.9693 StartZ=0 EndX=16.3876 EndY=-26.9693 EndZ=0
    g9: LineSegment [constr] StartX=16.3876 StartY=-26.9693 StartZ=0 EndX=32.7753 EndY=-26.9693 EndZ=0
  constraints (23):
    c: PointOnObject(g0,g-2)
    c: Radius(g0) = 18.5
    c: Diameter(g1) = 11
    c: Equal(g1,g2)
    c: Equal(g2,g3)
    c: Equal(g3,g4)
    c: Equal(g4,g5)
    c: Horizontal(g1,g2)
    c: Horizontal(g2,g3)
    c: Horizontal(g3,g4)
    c: Horizontal(g4,g5)
    c: Vertical(g0,g3)
    c: Coincident(g6,g1)
    c: Coincident(g6,g2)
    c: Coincident(g7,g2)
    c: Coincident(g7,g3)
    c: Coincident(g8,g3)
    c: Coincident(g8,g4)
    c: Coincident(g9,g4)
    c: Coincident(g9,g5)
    c: Equal(g9,g8)
    c: Equal(g8,g7)
    c: Equal(g7,g6)
FEATURE [PartDesign::Pocket] Pocket004
  BaseFeature = -> Fillet004
  Direction = (0,8.987e-12,-1)
  Length = 5
  Length2 = 5
  Placement = pos=(0,2.33659e-09,-260) rot=(0,0,1;0rad)
  Profile = -> Sketch036
  ReferenceAxis = -> Sketch036 [N_Axis]
  Refine = true
  Suppressed = false
  Type = 0
FEATURE [Sketcher::SketchObject] Sketch037
  ArcFitTolerance = 1e-06
  AttachmentSupport = -> [Pocket004]
  ExternalGeometry = -> [Pocket004]
  FullyConstrained = true
  MakeInternals = false
  MapMode = 5
  Placement = pos=(-1.553e-13,5.07345e-09,-564.544) rot=(0,0,1;0rad)
  sketch-geometry (6):
    g0: Circle CenterX=0 CenterY=15.7896 CenterZ=0 NormalX=0 NormalY=0 NormalZ=1 AngleXU=0 Radius=17.5
    g1: Circle CenterX=-32.7753 CenterY=-26.9693 CenterZ=0 NormalX=0 NormalY=0 NormalZ=1 AngleXU=0 Radius=5
    g2: Circle CenterX=-16.3876 CenterY=-26.9693 CenterZ=0 NormalX=0 NormalY=0 NormalZ=1 AngleXU=0 Radius=5
    g3: Circle CenterX=0 CenterY=-26.9693 CenterZ=0 NormalX=0 NormalY=0 NormalZ=1 AngleXU=0 Radius=5
    g4: Circle CenterX=16.3876 CenterY=-26.9693 CenterZ=0 NormalX=0 NormalY=0 NormalZ=1 AngleXU=0 Radius=5
    g5: Circle CenterX=32.7753 CenterY=-26.9693 CenterZ=0 NormalX=0 NormalY=0 NormalZ=1 AngleXU=0 Radius=5
  constraints (12):
    c: Diameter(g0) = 35
    c: Coincident(g0,g-3)
    c: Diameter(g1) = 10
    c: Coincident(g1,g-8)
    c: Coincident(g2,g-7)
    c: Coincident(g3,g-6)
    c: Coincident(g4,g-5)
    c: Coincident(g5,g-4)
    c: Equal(g5,g4)
    c: Equal(g4,g3)
    c: Equal(g3,g2)
    c: Equal(g2,g1)
FEATURE [PartDesign::Pad] Pad023
  BaseFeature = -> Pocket004
  Direction = (0,-8.9867e-12,1)
  Length = 10
  Length2 = 10
  Placement = pos=(0,2.33659e-09,-260) rot=(0,0,1;0rad)
  Profile = -> Sketch037
  ReferenceAxis = -> Sketch037 [N_Axis]
  Refine = true
  Suppressed = false
  Type = 0
FEATURE [PartDesign::Fillet] Fillet005
  Base = -> Pad023 [Edge38,Edge36,Edge34,Edge42,Edge44]
  BaseFeature = -> Pad023
  Placement = pos=(0,2.33659e-09,-260) rot=(0,0,1;0rad)
  Radius = 1
  Refine = true
  SupportTransform = false
  Suppressed = false
  UseAllEdges = false
FEATURE [Sketcher::SketchObject] Sketch038
  ArcFitTolerance = 1e-06
  AttachmentSupport = -> [Fillet005]
  ExternalGeometry = -> [Fillet005]
  FullyConstrained = false
  MakeInternals = false
  MapMode = 5
  Placement = pos=(0,4.98354e-09,-554.544) rot=(0,0,1;0rad)
  sketch-geometry (4):
    g0: ArcOfCircle CenterX=-1.55e-13 CenterY=28.5871 CenterZ=0 NormalX=0 NormalY=0 NormalZ=1 AngleXU=0 Radius=3.94672 StartAngle=3e-16 EndAngle=3.14159
    g1: ArcOfCircle CenterX=-1.553e-13 CenterY=2.99207 CenterZ=0 NormalX=0 NormalY=0 NormalZ=1 AngleXU=0 Radius=3.94672 StartAngle=3.14159 EndAngle=6.28319
    g2: LineSegment StartX=3.94672 StartY=28.5871 StartZ=0 EndX=3.94672 EndY=2.99207 EndZ=0
    g3: LineSegment StartX=-3.94672 StartY=28.5871 StartZ=0 EndX=-3.94672 EndY=2.99207 EndZ=0
  constraints (7):
    c: Tangent(g0,g2) = 1.5708
    c: Tangent(g0,g3) = -1.5708
    c: Tangent(g1,g2) = 1.5708
    c: Tangent(g1,g3) = -1.5708
    c: Equal(g0,g1)
    c: Symmetric(g0,g1,g-3)
    c: Vertical(g0,g1)
FEATURE [PartDesign::Pad] Pad024
  BaseFeature = -> Fillet005
  Direction = (0,-8.9866e-12,1)
  Length = 5
  Length2 = 10
  Placement = pos=(0,2.33659e-09,-260) rot=(0,0,1;0rad)
  Profile = -> Sketch038
  ReferenceAxis = -> Sketch038 [N_Axis]
  Refine = true
  Suppressed = false
  Type = 0
FEATURE [PartDesign::Fillet] Fillet006
  Base = -> Pad024 [Edge52]
  BaseFeature = -> Pad024
  Placement = pos=(0,2.33659e-09,-260) rot=(0,0,1;0rad)
  Radius = 0.5
  Refine = true
  SupportTransform = false
  Suppressed = false
  UseAllEdges = false
FEATURE [PartDesign::Fillet] Fillet007
  Base = -> Fillet006 [Edge17]
  BaseFeature = -> Fillet006
  Placement = pos=(0,2.33659e-09,-260) rot=(0,0,1;0rad)
  Radius = 1.5
  Refine = true
  SupportTransform = false
  Suppressed = false
  UseAllEdges = false
FEATURE [PartDesign::Fillet] Fillet008
  Base = -> Fillet006 [Edge5]
  BaseFeature = -> Fillet006
  Placement = pos=(0,2.33659e-09,-260) rot=(0,0,1;0rad)
  Radius = 0.5
  Refine = true
  SupportTransform = false
  Suppressed = false
  UseAllEdges = false
FEATURE [PartDesign::Plane] DatumPlane006
  AttachmentOffset = pos=(0,0,-3) rot=(0,0,1;0rad)
  AttachmentSupport = -> [Pad011]
  Length = 152.011
  MapMode = 5
  Placement = pos=(0,179.5,-3.95e-14) rot=(0,0.707107,0.707107;3.14159rad)
  ResizeMode = 0
  Width = 173.246
FEATURE [Sketcher::SketchObject] Sketch039
  ArcFitTolerance = 1e-06
  AttachmentSupport = -> [DatumPlane006]
  ExternalGeometry = -> [Pad011]
  FullyConstrained = false
  MakeInternals = false
  MapMode = 5
  Placement = pos=(0,179.5,-3.95e-14) rot=(0,0.707107,0.707107;3.14159rad)
  sketch-geometry (95):
    g0: LineSegment StartX=-52.1324 StartY=0.5 StartZ=0 EndX=-52.1324 EndY=-0.5 EndZ=0
    g1: LineSegment StartX=-52.1324 StartY=-0.5 StartZ=0 EndX=52.1324 EndY=-0.5 EndZ=0
    g2: LineSegment StartX=52.1324 StartY=-0.5 StartZ=0 EndX=52.1324 EndY=0.5 EndZ=0
    g3: LineSegment StartX=52.1324 StartY=0.5 StartZ=0 EndX=-52.1324 EndY=0.5 EndZ=0
    g4: LineSegment StartX=-51.8175 StartY=5.65 StartZ=0 EndX=-51.8175 EndY=4.65 EndZ=0
    g5: LineSegment StartX=-51.8175 StartY=4.65 StartZ=0 EndX=51.8175 EndY=4.65 EndZ=0
    g6: LineSegment StartX=51.8175 StartY=4.65 StartZ=0 EndX=51.8175 EndY=5.65 EndZ=0
    g7: LineSegment StartX=51.8175 StartY=5.65 StartZ=0 EndX=-51.8175 EndY=5.65 EndZ=0
    g8: LineSegment StartX=50.8077 StartY=9.8 StartZ=0 EndX=50.8077 EndY=10.8 EndZ=0
    g9: LineSegment StartX=50.8077 StartY=10.8 StartZ=0 EndX=-50.8077 EndY=10.8 EndZ=0
    g10: LineSegment StartX=-50.8077 StartY=10.8 StartZ=0 EndX=-50.8077 EndY=9.8 EndZ=0
    g11: LineSegment StartX=-50.8077 StartY=9.8 StartZ=0 EndX=50.8077 EndY=9.8 EndZ=0
    g12: LineSegment StartX=-50.1093 StartY=14.95 StartZ=0 EndX=50.1093 EndY=14.95 EndZ=0
    g13: LineSegment StartX=50.1093 StartY=14.95 StartZ=0 EndX=50.1093 EndY=15.95 EndZ=0
    g14: LineSegment StartX=50.1093 StartY=15.95 StartZ=0 EndX=-50.1093 EndY=15.95 EndZ=0
    g15: LineSegment StartX=-50.1093 StartY=15.95 StartZ=0 EndX=-50.1093 EndY=14.95 EndZ=0
    g16: LineSegment StartX=48.6484 StartY=20.1 StartZ=0 EndX=48.6484 EndY=21.1 EndZ=0
    g17: LineSegment StartX=48.6484 StartY=21.1 StartZ=0 EndX=-48.6484 EndY=21.1 EndZ=0
    g18: LineSegment StartX=-48.6484 StartY=21.1 StartZ=0 EndX=-48.6484 EndY=20.1 EndZ=0
    g19: LineSegment StartX=-48.6484 StartY=20.1 StartZ=0 EndX=48.6484 EndY=20.1 EndZ=0
    g20: LineSegment StartX=-45.7614 StartY=25.25 StartZ=0 EndX=45.7614 EndY=25.25 EndZ=0
    g21: LineSegment StartX=45.7614 StartY=25.25 StartZ=0 EndX=45.7614 EndY=26.25 EndZ=0
    g22: LineSegment StartX=45.7614 StartY=26.25 StartZ=0 EndX=-45.7614 EndY=26.25 EndZ=0
    g23: LineSegment StartX=-45.7614 StartY=26.25 StartZ=0 EndX=-45.7614 EndY=25.25 EndZ=0
    g24: LineSegment StartX=42.5781 StartY=30.4 StartZ=0 EndX=42.5781 EndY=31.4 EndZ=0
    g25: LineSegment StartX=42.5781 StartY=31.4 StartZ=0 EndX=-42.5781 EndY=31.4 EndZ=0
    g26: LineSegment StartX=-42.5781 StartY=31.4 StartZ=0 EndX=-42.5781 EndY=30.4 EndZ=0
    g27: LineSegment StartX=-42.5781 StartY=30.4 StartZ=0 EndX=42.5781 EndY=30.4 EndZ=0
    g28: LineSegment StartX=-38.6581 StartY=35.55 StartZ=0 EndX=38.6581 EndY=35.55 EndZ=0
    g29: LineSegment StartX=38.6581 StartY=35.55 StartZ=0 EndX=38.6581 EndY=36.55 EndZ=0
    g30: LineSegment StartX=38.6581 StartY=36.55 StartZ=0 EndX=-38.6581 EndY=36.55 EndZ=0
    g31: LineSegment StartX=-38.6581 StartY=36.55 StartZ=0 EndX=-38.6581 EndY=35.55 EndZ=0
    g32: LineSegment StartX=33.3164 StartY=40.7 StartZ=0 EndX=33.3164 EndY=41.7 EndZ=0
    g33: LineSegment StartX=33.3164 StartY=41.7 StartZ=0 EndX=-33.3164 EndY=41.7 EndZ=0
    g34: LineSegment StartX=-33.3164 StartY=41.7 StartZ=0 EndX=-33.3164 EndY=40.7 EndZ=0
    g35: LineSegment StartX=-33.3164 StartY=40.7 StartZ=0 EndX=33.3164 EndY=40.7 EndZ=0
    g36: LineSegment StartX=-25.4607 StartY=45.85 StartZ=0 EndX=25.4607 EndY=45.85 EndZ=0
    g37: LineSegment StartX=25.4607 StartY=45.85 StartZ=0 EndX=25.4607 EndY=46.85 EndZ=0
    g38: LineSegment StartX=25.4607 StartY=46.85 StartZ=0 EndX=-25.4607 EndY=46.85 EndZ=0
    g39: LineSegment StartX=-25.4607 StartY=46.85 StartZ=0 EndX=-25.4607 EndY=45.85 EndZ=0
    g40: LineSegment [constr] StartX=0 StartY=51 StartZ=0 EndX=0 EndY=46.85 EndZ=0
    g41: LineSegment [constr] StartX=3e-16 StartY=45.85 StartZ=0 EndX=3e-16 EndY=41.7 EndZ=0
    g42: LineSegment [constr] StartX=-2.7e-15 StartY=40.7 StartZ=0 EndX=-2.7e-15 EndY=36.55 EndZ=0
    g43: LineSegment [constr] StartX=1.1e-15 StartY=35.55 StartZ=0 EndX=1.1e-15 EndY=31.4 EndZ=0
    g44: LineSegment [constr] StartX=1e-15 StartY=30.4 StartZ=0 EndX=1e-15 EndY=26.25 EndZ=0
    g45: LineSegment [constr] StartX=1.9e-15 StartY=25.25 StartZ=0 EndX=1.9e-15 EndY=21.1 EndZ=0
    g46: LineSegment [constr] StartX=-2.8e-15 StartY=20.1 StartZ=0 EndX=-2.8e-15 EndY=15.95 EndZ=0
    g47: LineSegment [constr] StartX=3.3e-15 StartY=14.95 StartZ=0 EndX=3.3e-15 EndY=10.8 EndZ=0
    g48: LineSegment [constr] StartX=-2e-16 StartY=9.8 StartZ=0 EndX=-2e-16 EndY=5.65 EndZ=0
    g49: LineSegment [constr] StartX=-2.8e-15 StartY=4.65 StartZ=0 EndX=-2.8e-15 EndY=0.5 EndZ=0
    g50: LineSegment StartX=-52.2778 StartY=-4.65 StartZ=0 EndX=-52.2778 EndY=-5.65 EndZ=0
    g51: LineSegment StartX=-52.2778 StartY=-5.65 StartZ=0 EndX=52.2778 EndY=-5.65 EndZ=0
    g52: LineSegment StartX=52.2778 StartY=-5.65 StartZ=0 EndX=52.2778 EndY=-4.65 EndZ=0
    g53: LineSegment StartX=52.2778 StartY=-4.65 StartZ=0 EndX=-52.2778 EndY=-4.65 EndZ=0
    g54: LineSegment StartX=52.0593 StartY=-9.8 StartZ=0 EndX=-52.0593 EndY=-9.8 EndZ=0
    g55: LineSegment StartX=-52.0593 StartY=-9.8 StartZ=0 EndX=-52.0593 EndY=-10.8 EndZ=0
    g56: LineSegment StartX=-52.0593 StartY=-10.8 StartZ=0 EndX=52.0593 EndY=-10.8 EndZ=0
    g57: LineSegment StartX=52.0593 StartY=-10.8 StartZ=0 EndX=52.0593 EndY=-9.8 EndZ=0
    g58: LineSegment StartX=-50.2273 StartY=-14.95 StartZ=0 EndX=-50.2273 EndY=-15.95 EndZ=0
    g59: LineSegment StartX=-50.2273 StartY=-15.95 StartZ=0 EndX=50.2273 EndY=-15.95 EndZ=0
    g60: LineSegment StartX=50.2273 StartY=-15.95 StartZ=0 EndX=50.2273 EndY=-14.95 EndZ=0
    g61: LineSegment StartX=50.2273 StartY=-14.95 StartZ=0 EndX=-50.2273 EndY=-14.95 EndZ=0
    g62: LineSegment StartX=48.4014 StartY=-20.1 StartZ=0 EndX=-48.4014 EndY=-20.1 EndZ=0
    g63: LineSegment StartX=-48.4014 StartY=-20.1 StartZ=0 EndX=-48.4014 EndY=-21.1 EndZ=0
    g64: LineSegment StartX=-48.4014 StartY=-21.1 StartZ=0 EndX=48.4014 EndY=-21.1 EndZ=0
    g65: LineSegment StartX=48.4014 StartY=-21.1 StartZ=0 EndX=48.4014 EndY=-20.1 EndZ=0
    g66: LineSegment StartX=-46.0334 StartY=-25.25 StartZ=0 EndX=-46.0334 EndY=-26.25 EndZ=0
    g67: LineSegment StartX=-46.0334 StartY=-26.25 StartZ=0 EndX=46.0334 EndY=-26.25 EndZ=0
    g68: LineSegment StartX=46.0334 StartY=-26.25 StartZ=0 EndX=46.0334 EndY=-25.25 EndZ=0
    g69: LineSegment StartX=46.0334 StartY=-25.25 StartZ=0 EndX=-46.0334 EndY=-25.25 EndZ=0
    g70: LineSegment StartX=42.7931 StartY=-30.4 StartZ=0 EndX=-42.7931 EndY=-30.4 EndZ=0
    g71: LineSegment StartX=-42.7931 StartY=-30.4 StartZ=0 EndX=-42.7931 EndY=-31.4 EndZ=0
    g72: LineSegment StartX=-42.7931 StartY=-31.4 StartZ=0 EndX=42.7931 EndY=-31.4 EndZ=0
    g73: LineSegment StartX=42.7931 StartY=-31.4 StartZ=0 EndX=42.7931 EndY=-30.4 EndZ=0
    g74: LineSegment StartX=-38.2654 StartY=-35.55 StartZ=0 EndX=-38.2654 EndY=-36.55 EndZ=0
    g75: LineSegment StartX=-38.2654 StartY=-36.55 StartZ=0 EndX=38.2654 EndY=-36.55 EndZ=0
    g76: LineSegment StartX=38.2654 StartY=-36.55 StartZ=0 EndX=38.2654 EndY=-35.55 EndZ=0
    g77: LineSegment StartX=38.2654 StartY=-35.55 StartZ=0 EndX=-38.2654 EndY=-35.55 EndZ=0
    g78: LineSegment StartX=32.9949 StartY=-40.7 StartZ=0 EndX=-32.9949 EndY=-40.7 EndZ=0
    g79: LineSegment StartX=-32.9949 StartY=-40.7 StartZ=0 EndX=-32.9949 EndY=-41.7 EndZ=0
    g80: LineSegment StartX=-32.9949 StartY=-41.7 StartZ=0 EndX=32.9949 EndY=-41.7 EndZ=0
    g81: LineSegment StartX=32.9949 StartY=-41.7 StartZ=0 EndX=32.9949 EndY=-40.7 EndZ=0
    g82: LineSegment StartX=-25 StartY=-45.85 StartZ=0 EndX=-25 EndY=-46.85 EndZ=0
    g83: LineSegment StartX=-25 StartY=-46.85 StartZ=0 EndX=25 EndY=-46.85 EndZ=0
    g84: LineSegment StartX=25 StartY=-46.85 StartZ=0 EndX=25 EndY=-45.85 EndZ=0
    g85: LineSegment StartX=25 StartY=-45.85 StartZ=0 EndX=-25 EndY=-45.85 EndZ=0
    g86: LineSegment [constr] StartX=3.2e-15 StartY=-0.5 StartZ=0 EndX=3.2e-15 EndY=-4.65 EndZ=0
    g87: LineSegment [constr] StartX=-3.2e-15 StartY=-5.65 StartZ=0 EndX=-3.2e-15 EndY=-9.8 EndZ=0
    g88: LineSegment [constr] StartX=-3.5e-15 StartY=-10.8 StartZ=0 EndX=-3.5e-15 EndY=-14.95 EndZ=0
    g89: LineSegment [constr] StartX=-2.5e-15 StartY=-15.95 StartZ=0 EndX=-2.5e-15 EndY=-20.1 EndZ=0
    g90: LineSegment [constr] StartX=2e-16 StartY=-21.1 StartZ=0 EndX=2e-16 EndY=-25.25 EndZ=0
    g91: LineSegment [constr] StartX=-3.1e-15 StartY=-26.25 StartZ=0 EndX=-3.1e-15 EndY=-30.4 EndZ=0
    g92: LineSegment [constr] StartX=1.9e-15 StartY=-31.4 StartZ=0 EndX=1.9e-15 EndY=-35.55 EndZ=0
    g93: LineSegment [constr] StartX=-2.9e-15 StartY=-36.55 StartZ=0 EndX=-2.9e-15 EndY=-40.7 EndZ=0
    g94: LineSegment [constr] StartX=-1.8e-15 StartY=-41.7 StartZ=0 EndX=-1.8e-15 EndY=-45.85 EndZ=0
  constraints (248):
    c: Coincident(g0,g1)
    c: Coincident(g1,g2)
    c: Coincident(g2,g3)
    c: Coincident(g3,g0)
    c: Vertical(g2)
    c: Horizontal(g1)
    c: Horizontal(g3)
    c: Symmetric(g0,g0,g-1)
    c: DistanceY(g0,g0) = 1
    c: Coincident(g4,g5)
    c: Coincident(g5,g6)
    c: Coincident(g6,g7)
    c: Coincident(g7,g4)
    c: Vertical(g4)
    c: Vertical(g6)
    c: Horizontal(g5)
    c: Horizontal(g7)
    c: Coincident(g8,g9)
    c: Coincident(g9,g10)
    c: Coincident(g10,g11)
    c: Coincident(g11,g8)
    c: Vertical(g8)
    c: Vertical(g10)
    c: Horizontal(g9)
    c: Horizontal(g11)
    c: Coincident(g12,g13)
    c: Coincident(g13,g14)
    c: Coincident(g14,g15)
    c: Coincident(g15,g12)
    c: Horizontal(g12)
    c: Horizontal(g14)
    c: Vertical(g13)
    c: Vertical(g15)
    c: Coincident(g16,g17)
    c: Coincident(g17,g18)
    c: Coincident(g18,g19)
    c: Coincident(g19,g16)
    c: Vertical(g16)
    c: Vertical(g18)
    c: Horizontal(g17)
    c: Horizontal(g19)
    c: Coincident(g20,g21)
    c: Coincident(g21,g22)
    c: Coincident(g22,g23)
    c: Coincident(g23,g20)
    c: Horizontal(g20)
    c: Horizontal(g22)
    c: Vertical(g21)
    c: Vertical(g23)
    c: Coincident(g24,g25)
    c: Coincident(g25,g26)
    c: Coincident(g26,g27)
    c: Coincident(g27,g24)
    c: Vertical(g24)
    c: Vertical(g26)
    c: Horizontal(g25)
    c: Horizontal(g27)
    c: Coincident(g28,g29)
    c: Coincident(g29,g30)
    c: Coincident(g30,g31)
    c: Coincident(g31,g28)
    c: Horizontal(g28)
    c: Horizontal(g30)
    c: Vertical(g29)
    c: Vertical(g31)
    c: Coincident(g32,g33)
    c: Coincident(g33,g34)
    c: Coincident(g34,g35)
    c: Coincident(g35,g32)
    c: Vertical(g32)
    c: Vertical(g34)
    c: Horizontal(g33)
    c: Horizontal(g35)
    c: Coincident(g36,g37)
    c: Coincident(g37,g38)
    c: Coincident(g38,g39)
    c: Coincident(g39,g36)
    c: Horizontal(g36)
    c: Horizontal(g38)
    c: Vertical(g37)
    c: Vertical(g39)
    c: PointOnObject(g40,g-3)
    c: Symmetric(g38,g38,g40)
    c: PointOnObject(g40,g-2)
    c: Vertical(g40)
    c: Symmetric(g36,g36,g41)
    c: Symmetric(g33,g33,g41)
    c: Vertical(g41)
    c: Symmetric(g35,g35,g42)
    c: Symmetric(g30,g30,g42)
    c: Vertical(g42)
    c: Symmetric(g28,g28,g43)
    c: Symmetric(g25,g25,g43)
    c: Vertical(g43)
    c: Symmetric(g27,g27,g44)
    c: Symmetric(g22,g22,g44)
    c: Symmetric(g20,g20,g45)
    c: Symmetric(g17,g17,g45)
    c: Symmetric(g19,g19,g46)
    c: Symmetric(g14,g14,g46)
    c: Vertical(g46)
    c: Symmetric(g12,g12,g47)
    c: Symmetric(g9,g9,g47)
    c: Symmetric(g11,g11,g48)
    c: Symmetric(g7,g7,g48)
    c: Symmetric(g5,g5,g49)
    c: Symmetric(g3,g3,g49)
    c: Equal(g46,g47)
    c: Equal(g47,g48)
    c: Equal(g48,g49)
    c: Equal(g49,g44)
    c: Equal(g44,g45)
    c: Equal(g45,g43)
    c: Equal(g43,g42)
    c: Equal(g42,g41)
    c: Equal(g41,g40)
    c: Equal(g39,g34)
    c: Equal(g34,g31)
    c: Equal(g31,g26)
    c: Equal(g26,g23)
    c: Equal(g23,g18)
    c: Equal(g18,g15)
    c: Equal(g15,g10)
    c: Equal(g10,g4)
    c: Equal(g4,g0)
    c: Vertical(g49)
    c: Vertical(g48)
    c: Vertical(g47)
    c: Vertical(g45)
    c: Vertical(g44)
    c: Coincident(g50,g51)
    c: Coincident(g51,g52)
    c: Coincident(g52,g53)
    c: Coincident(g53,g50)
    c: Vertical(g50)
    c: Vertical(g52)
    c: Horizontal(g51)
    c: Horizontal(g53)
    c: Coincident(g54,g55)
    c: Coincident(g55,g56)
    c: Coincident(g56,g57)
    c: Coincident(g57,g54)
    c: Horizontal(g54)
    c: Horizontal(g56)
    c: Vertical(g55)
    c: Vertical(g57)
    c: Coincident(g58,g59)
    c: Coincident(g59,g60)
    c: Coincident(g60,g61)
    c: Coincident(g61,g58)
    c: Vertical(g58)
    c: Vertical(g60)
    c: Horizontal(g59)
    c: Horizontal(g61)
    c: Coincident(g62,g63)
    c: Coincident(g63,g64)
    c: Coincident(g64,g65)
    c: Coincident(g65,g62)
    c: Horizontal(g62)
    c: Horizontal(g64)
    c: Vertical(g63)
    c: Vertical(g65)
    c: Coincident(g66,g67)
    c: Coincident(g67,g68)
    c: Coincident(g68,g69)
    c: Coincident(g69,g66)
    c: Vertical(g66)
    c: Vertical(g68)
    c: Horizontal(g67)
    c: Horizontal(g69)
    c: Coincident(g70,g71)
    c: Coincident(g71,g72)
    c: Coincident(g72,g73)
    c: Coincident(g73,g70)
    c: Horizontal(g70)
    c: Horizontal(g72)
    c: Vertical(g71)
    c: Vertical(g73)
    c: Coincident(g74,g75)
    c: Coincident(g75,g76)
    c: Coincident(g76,g77)
    c: Coincident(g77,g74)
    c: Vertical(g74)
    c: Vertical(g76)
    c: Horizontal(g75)
    c: Horizontal(g77)
    c: Coincident(g78,g79)
    c: Coincident(g79,g80)
    c: Coincident(g80,g81)
    c: Coincident(g81,g78)
    c: Horizontal(g78)
    c: Horizontal(g80)
    c: Vertical(g79)
    c: Vertical(g81)
    c: Coincident(g82,g83)
    c: Coincident(g83,g84)
    c: Coincident(g84,g85)
    c: Coincident(g85,g82)
    c: Vertical(g82)
    c: Vertical(g84)
    c: Horizontal(g83)
    c: Horizontal(g85)
    c: Equal(g0,g50)
    c: Equal(g50,g55)
    c: Equal(g55,g58)
    c: Equal(g58,g63)
    c: Equal(g63,g66)
    c: Equal(g66,g71)
    c: Equal(g71,g74)
    c: Equal(g74,g79)
    c: Equal(g79,g82)
    c: Symmetric(g1,g1,g86)
    c: Symmetric(g53,g53,g86)
    c: Vertical(g86)
    c: Symmetric(g51,g51,g87)
    c: Symmetric(g54,g54,g87)
    c: Symmetric(g56,g56,g88)
    c: Symmetric(g61,g61,g88)
    c: Symmetric(g59,g59,g89)
    c: Symmetric(g62,g62,g89)
    c: Vertical(g89)
    c: Symmetric(g64,g64,g90)
    c: Symmetric(g69,g69,g90)
    c: Symmetric(g67,g67,g91)
    c: Symmetric(g70,g70,g91)
    c: Symmetric(g72,g72,g92)
    c: Symmetric(g77,g77,g92)
    c: Symmetric(g75,g75,g93)
    c: Symmetric(g78,g78,g93)
    c: Symmetric(g80,g80,g94)
    c: Symmetric(g85,g85,g94)
    c: Vertical(g92)
    c: Vertical(g93)
    c: Vertical(g94)
    c: Vertical(g87)
    c: Vertical(g88)
    c: Vertical(g90)
    c: Vertical(g91)
    c: Equal(g86,g87)
    c: Equal(g87,g88)
    c: Equal(g88,g89)
    c: Equal(g89,g90)
    c: Equal(g90,g91)
    c: Equal(g91,g92)
    c: Equal(g92,g93)
    c: Equal(g93,g94)
    c: Equal(g49,g86)
    c: DistanceX(g83,g83) = 50
FEATURE [PartDesign::Pad] Pad025
  BaseFeature = -> Pad011
  Direction = (0,1,-2e-16)
  Length = 2
  Length2 = 10
  Profile = -> Sketch039
  ReferenceAxis = -> Sketch039 [N_Axis]
  Refine = true
  Reversed = true
  Suppressed = false
  Type = 0
FEATURE [Sketcher::SketchObject] Sketch040
  ArcFitTolerance = 1e-06
  AttachmentSupport = -> [DatumPlane006]
  ExternalGeometry = -> [Pad025]
  FullyConstrained = true
  MakeInternals = false
  MapMode = 5
  Placement = pos=(0,179.5,-3.95e-14) rot=(0,0.707107,0.707107;3.14159rad)
  sketch-geometry (6):
    g0: Circle CenterX=0 CenterY=0 CenterZ=0 NormalX=0 NormalY=0 NormalZ=1 AngleXU=0 Radius=41.7
    g1: Circle CenterX=0 CenterY=0 CenterZ=0 NormalX=0 NormalY=0 NormalZ=1 AngleXU=0 Radius=40.7
    g2: Circle CenterX=0 CenterY=0 CenterZ=0 NormalX=0 NormalY=0 NormalZ=1 AngleXU=0 Radius=31.4
    g3: Circle CenterX=0 CenterY=0 CenterZ=0 NormalX=0 NormalY=0 NormalZ=1 AngleXU=0 Radius=30.4
    g4: Circle CenterX=0 CenterY=0 CenterZ=0 NormalX=0 NormalY=0 NormalZ=1 AngleXU=0 Radius=21.1
    g5: Circle CenterX=0 CenterY=0 CenterZ=0 NormalX=0 NormalY=0 NormalZ=1 AngleXU=0 Radius=4.65
  constraints (12):
    c: Coincident(g0,g-1)
    c: Coincident(g2,g1)
    c: Coincident(g3,g0)
    c: Coincident(g4,g0)
    c: Tangent(g0,g-3)
    c: Tangent(g1,g-4)
    c: Tangent(g2,g-5)
    c: Tangent(g3,g-6)
    c: Coincident(g5,g1)
    c: Coincident(g0,g1)
    c: Tangent(g4,g-8)
    c: Tangent(g5,g-9)
FEATURE [PartDesign::Pad] Pad026
  BaseFeature = -> Pad025
  Direction = (0,1,-2e-16)
  Length = 2
  Length2 = 10
  Profile = -> Sketch040
  ReferenceAxis = -> Sketch040 [N_Axis]
  Refine = true
  Reversed = true
  Suppressed = false
  Type = 0
FEATURE [PartDesign::Plane] DatumPlane007
  AttachmentOffset = pos=(0,0,-0.5) rot=(0,0,1;0rad)
  AttachmentSupport = -> [Pad026]
  Length = 152.011
  MapMode = 5
  Placement = pos=(0,179,1e-16) rot=(0,0.707107,0.707107;3.14159rad)
  ResizeMode = 0
  Width = 173.246
FEATURE [Sketcher::SketchObject] Sketch041
  ArcFitTolerance = 1e-06
  AttachmentSupport = -> [DatumPlane007]
  FullyConstrained = false
  MakeInternals = false
  MapMode = 5
  Placement = pos=(0,179,1e-16) rot=(0,0.707107,0.707107;3.14159rad)
  sketch-geometry (4):
    g0: LineSegment StartX=-6 StartY=52.2557 StartZ=0 EndX=-6 EndY=-52.1051 EndZ=0
    g1: LineSegment StartX=-6 StartY=-52.1051 StartZ=0 EndX=6 EndY=-52.1051 EndZ=0
    g2: LineSegment StartX=6 StartY=-52.1051 StartZ=0 EndX=6 EndY=52.2557 EndZ=0
    g3: LineSegment StartX=6 StartY=52.2557 StartZ=0 EndX=-6 EndY=52.2557 EndZ=0
  constraints (9):
    c: Coincident(g0,g1)
    c: Coincident(g1,g2)
    c: Coincident(g2,g3)
    c: Coincident(g3,g0)
    c: Vertical(g0)
    c: Vertical(g2)
    c: Horizontal(g1)
    c: Symmetric(g2,g0,g-2)
    c: DistanceX(g3,g3) = 12
FEATURE [PartDesign::Pad] Pad027
  BaseFeature = -> Pad026
  Direction = (0,1,-2e-16)
  Length = 1
  Length2 = 10
  Profile = -> Sketch041
  ReferenceAxis = -> Sketch041 [N_Axis]
  Refine = true
  Reversed = true
  Suppressed = false
  Type = 0
FEATURE [Sketcher::SketchObject] Sketch042
  ArcFitTolerance = 1e-06
  AttachmentSupport = -> [Pad027]
  FullyConstrained = false
  MakeInternals = false
  MapMode = 5
  Placement = pos=(0,179.5,0) rot=(0,0.707107,0.707107;3.14159rad)
  sketch-geometry (1):
    g0: Circle CenterX=0 CenterY=0 CenterZ=0 NormalX=0 NormalY=0 NormalZ=1 AngleXU=0 Radius=4.86337
  constraints (1):
    c: Coincident(g0,g-1)
FEATURE [PartDesign::Pocket] Pocket005
  BaseFeature = -> Pad027
  Direction = (0,-1,2e-16)
  Length = 2
  Length2 = 5
  Profile = -> Sketch042
  ReferenceAxis = -> Sketch042 [N_Axis]
  Refine = true
  Suppressed = false
  Type = 0
FEATURE [Sketcher::SketchObject] Sketch043
  ArcFitTolerance = 1e-06
  AttachmentSupport = -> [Pocket005]
  FullyConstrained = false
  MakeInternals = false
  MapMode = 5
  Placement = pos=(0,4.6e-15,20.7565) rot=(0,0,1;0rad)
  sketch-geometry (1):
    g0: Circle CenterX=11.6269 CenterY=115.247 CenterZ=0 NormalX=0 NormalY=0 NormalZ=1 AngleXU=0 Radius=7.5
  constraints (1):
    c: Diameter(g0) = 15
FEATURE [PartDesign::Pocket] Pocket006
  BaseFeature = -> Pocket005
  Direction = (0,0,-1)
  Length = 0
  Length2 = 5
  Profile = -> Sketch043
  ReferenceAxis = -> Sketch043 [N_Axis]
  Refine = true
  Reversed = true
  Suppressed = false
  Type = 3
  UpToFace = -> Pocket005 [Face10]
FEATURE [Sketcher::SketchObject] Sketch044
  ArcFitTolerance = 1e-06
  AttachmentSupport = -> [Pocket006]
  ExternalGeometry = -> [Pocket006]
  FullyConstrained = false
  MakeInternals = false
  MapMode = 5
  Placement = pos=(0,0,20.7565) rot=(0,0,1;0rad)
  sketch-geometry (1):
    g0: Circle CenterX=11.7186 CenterY=115.302 CenterZ=0 NormalX=0 NormalY=0 NormalZ=1 AngleXU=0 Radius=5
  constraints (1):
    c: Diameter(g0) = 10
FEATURE [PartDesign::Pad] Pad028
  BaseFeature = -> Pocket006
  Direction = (0,0,1)
  Length = 50
  Length2 = 10
  Profile = -> Sketch044
  ReferenceAxis = -> Sketch044 [N_Axis]
  Refine = true
  Suppressed = false
  Type = 0
FEATURE [Sketcher::SketchObject] Sketch045
  ArcFitTolerance = 1e-06
  AttachmentSupport = -> [Pad028]
  ExternalGeometry = -> [Pad028]
  FullyConstrained = true
  MakeInternals = false
  MapMode = 5
  Placement = pos=(0,0,70.7565) rot=(0,0,1;0rad)
  sketch-geometry (1):
    g0: Circle CenterX=11.7186 CenterY=115.302 CenterZ=0 NormalX=0 NormalY=0 NormalZ=1 AngleXU=0 Radius=8
  constraints (2):
    c: Diameter(g0) = 16
    c: Coincident(g0,g-3)
FEATURE [PartDesign::Pad] Pad029
  BaseFeature = -> Pad028
  Direction = (0,0,1)
  Length = 7
  Length2 = 10
  Profile = -> Sketch045
  ReferenceAxis = -> Sketch045 [N_Axis]
  Refine = true
  Suppressed = false
  Type = 0
FEATURE [PartDesign::Fillet] Fillet009
  Base = -> Pad029 [Edge1196]
  BaseFeature = -> Pad029
  Radius = 5
  Refine = true
  SupportTransform = false
  Suppressed = false
  UseAllEdges = false
FEATURE [PartDesign::Pad] Pad005
  BaseFeature = -> Pad003
  Direction = (0,1,-2e-16)
  Length = 25
  Length2 = 10
  Profile = -> Sketch012
  ReferenceAxis = -> Sketch012 [N_Axis]
  Refine = true
  Suppressed = false
  Type = 3
  UpToFace = -> Fillet009 [Face370]
FEATURE [PartDesign::Body] Body
  AllowCompound = false
  Group = -> [Sketch,Pad,DatumPlane,CopyFace,DatumPlane001,CopyFace001,Sketch001,Sketch002,Sketch003,Sketch004,Boolean,Sketch005,Boolean001,Sketch006,Pad001,Sketch007,Pad002,Chamfer,Sketch008,Pad003,DatumPlane002,Sketch012,Pad005]
  Origin = -> Origin
  Tip = -> Pad005
FEATURE [PartDesign::Body] Body003
  AllowCompound = false
  Group = -> [CopyBoolean002,Sketch015,Pad008,Sketch016,Pad009,Sketch017,Pad010,Sketch018,Pocket,Sketch019,Pad011,Sketch020,DatumPlane006,Sketch039,Pad025,Sketch040,Pad026,DatumPlane007,Sketch041,Pad027,Sketch042,Pocket005,Sketch043,Pocket006,Sketch044,Pad028,Sketch045,Pad029,Fillet009]
  Origin = -> Origin003
  Tip = -> Fillet009
FEATURE [PartDesign::Chamfer] Chamfer001
  Angle = 45
  Base = -> Fillet008 [Edge43]
  BaseFeature = -> Fillet008
  ChamferType = 0
  FlipDirection = false
  Placement = pos=(0,2.33659e-09,-260) rot=(0,0,1;0rad)
  Refine = true
  Size = 15
  Size2 = 1
  SupportTransform = false
  Suppressed = false
  UseAllEdges = false
FEATURE [Part::FeaturePython] Array003  # Draft array (typed FeaturePython)
  AlwaysSyncPlacement = false
  Angle = 360
  ArrayType = 1
  Axis = (0,1,0)
  Base = -> Sweep
  Center = (0,0,0)
  Count = 100
  ExpandArray = false
  Fuse = false
  IntervalAxis = (0,0,0)
  IntervalX = (50,0,0)
  IntervalY = (0,50,0)
  IntervalZ = (0,0,50)
  NumberCircles = 3
  NumberPolar = 100
  NumberX = 2
  NumberY = 2
  NumberZ = 1
  PlacementList = 100 placements: [(0,0,0),(0,0,0),(0,0,0),(0,0,0),(0,0,0),(0,0,0),(0,0,0),(0,0,0),(0,0,0),(0,0,0),(0,0,0),(0,0,0),(0,0,0),(0,0,0),(0,0,0),(0,0,0),(0,0,0),(0,0,0),(0,0,0),(0,0,0),(0,0,0),(0,0,0),(0,0,0),(0,0,0),(0,0,0),(0,0,0),(0,0,0),(0,0,0),(0,0,0),(0,0,0),(0,0,0),(0,0,0),(0,0,0),(0,0,0),(0,0,0),(0,0,0),(0,0,0),(0,0,0),(0,0,0),(0,0,0),(0,0,0),(0,0,0),(0,0,0),(0,0,0),(0,0,0),(0,0,0),(0,0,0),(0,0,0),(0,0,0),(0,0,0),+50 more]
  RadialDistance = 50
  ScaleList = (100) [(1,1,1),(1,1,1),(1,1,1),(1,1,1),(1,1,1),(1,1,1),(1,1,1),(1,1,1),(1,1,1),(1,1,1),(1,1,1),(1,1,1),(1,1,1),(1,1,1),(1,1,1),(1,1,1),(1,1,1),(1,1,1),+82 more]
  Symmetry = 1
  TangentialDistance = 25
FEATURE [PartDesign::Boolean] Boolean003
  BaseFeature = -> Pad004
  Group = -> [Array003]
  Refine = true
  Suppressed = false
  Type = 0
  UsePlacement = true
FEATURE [PartDesign::Body] Body001
  AllowCompound = false
  Group = -> [CopyDatumPlane002,Sketch009,Pad004,Boolean003]
  Origin = -> Origin001
  Tip = -> Boolean003
FEATURE [PartDesign::ShapeBinder] CopyBoolean003
  TraceSupport = false
FEATURE [PartDesign::Plane] DatumPlane008
  AttachmentOffset = pos=(0,0,-10) rot=(0,0,1;0rad)
  AttachmentSupport = -> [CopyBoolean003]
  Length = 369.532
  MapMode = 5
  Placement = pos=(0,-32.5,-2.2e-15) rot=(1,0,0;1.5708rad)
  ResizeMode = 0
  Width = 369.561
FEATURE [PartDesign::ShapeBinder] CopyBoolean004
  Placement = pos=(0,0,0) rot=(0,1,0;0.062832rad)
  TraceSupport = false
FEATURE [Sketcher::SketchObject] Sketch046
  ArcFitTolerance = 1e-06
  AttachmentSupport = -> [DatumPlane008]
  ExternalGeometry = -> [CopyBoolean004]
  FullyConstrained = false
  MakeInternals = false
  MapMode = 5
  Placement = pos=(0,-32.5,-2.2e-15) rot=(1,0,0;1.5708rad)
  sketch-geometry (2):
    g0: Circle CenterX=0 CenterY=0 CenterZ=0 NormalX=0 NormalY=0 NormalZ=1 AngleXU=0 Radius=151
    g1: Circle CenterX=0 CenterY=0 CenterZ=0 NormalX=0 NormalY=0 NormalZ=1 AngleXU=0 Radius=154
  constraints (2):
    c: Coincident(g0,g-1)
    c: Tangent(g0,g-3)
FEATURE [PartDesign::Line] DatumLine001
  AttacherType = Attacher::AttachEngineLine
  AttachmentSupport = -> [CopyBoolean004]
  Length = 20
  MapMode = 19
  Placement = pos=(149.704,-35,-9.41858) rot=(0.022216,-0.706932,0.706932;3.09717rad)
  ResizeMode = 0
FEATURE [PartDesign::Pad] Pad030
  Direction = (0,-1,2e-16)
  Length = 20
  Length2 = 10
  Placement = pos=(0,-32.5,-2.2e-15) rot=(1,0,0;1.5708rad)
  Profile = -> Sketch046
  ReferenceAxis = -> Sketch046 [N_Axis]
  Refine = true
  Reversed = true
  Suppressed = false
  Type = 0
FEATURE [PartDesign::Fillet] Fillet010
  Base = -> Pad030 [Edge2,Edge3]
  BaseFeature = -> Pad030
  Placement = pos=(0,-32.5,-2.2e-15) rot=(1,0,0;1.5708rad)
  Radius = 2
  Refine = true
  SupportTransform = false
  Suppressed = false
  UseAllEdges = false
FEATURE [PartDesign::Body] Body006
  AllowCompound = false
  Group = -> [DatumPlane008,CopyBoolean003,Sketch046,DatumLine001,CopyBoolean004,Pad030,Fillet010]
  Origin = -> Origin006
  Tip = -> Fillet010
FEATURE [Sketcher::SketchObject] Sketch047
  ArcFitTolerance = 1e-06
  AttachmentSupport = -> [Pad018]
  FullyConstrained = false
  MakeInternals = false
  MapMode = 5
  Placement = pos=(2.95e-14,8.54086e-10,-159.544) rot=(1,0,0;3.14159rad)
  sketch-geometry (1):
    g0: Circle CenterX=0 CenterY=-102.298 CenterZ=0 NormalX=0 NormalY=0 NormalZ=1 AngleXU=0 Radius=17.5
  constraints (2):
    c: PointOnObject(g0,g-2)
    c: Radius(g0) = 17.5
FEATURE [PartDesign::Pad] Pad031
  BaseFeature = -> Pad018
  Direction = (0,8.9862e-12,-1)
  Length = 140
  Length2 = 10
  Placement = pos=(0,0,-64.5) rot=(1,0,0;3.14159rad)
  Profile = -> Sketch047
  ReferenceAxis = -> Sketch047 [N_Axis]
  Refine = true
  Suppressed = false
  Type = 0
FEATURE [PartDesign::Body] Body004
  AllowCompound = false
  Group = -> [DatumLine,CopyPad011,Sketch021,DatumPlane004,CopyExtrude003,Pad012,Sketch022,Pad013,Sketch023,Pad014,Sketch024,Pocket001,Sketch025,Pocket002,Sketch026,Pocket003,Sketch027,Pad015,Sketch028,Pad016,Sketch029,Pad017,Sketch030,Pad018,Sketch047,Pad031]
  Origin = -> Origin004
  Tip = -> Pad031
FEATURE [PartDesign::ShapeBinder] CopyChamfer001
  Placement = pos=(-1.55e-13,5.07345e-09,-564.544) rot=(0,0,1;0rad)
  TraceSupport = false
FEATURE [PartDesign::Plane] DatumPlane009
  AttachmentSupport = -> [CopyChamfer001]
  Length = 69.0867
  MapMode = 11
  Placement = pos=(-1.563e-13,15.7896,-564.544) rot=(0,0,1;1.5708rad)
  ResizeMode = 0
  Width = 60.7972
FEATURE [PartDesign::ShapeBinder] CopyChamfer002
  Placement = pos=(0,4.93861e-09,-549.544) rot=(0,0,1;0rad)
  TraceSupport = false
FEATURE [PartDesign::Line] DatumLine002
  AttacherType = Attacher::AttachEngineLine
  AttachmentSupport = -> [CopyChamfer002]
  Length = 20
  MapMode = 29
  Placement = pos=(-3.94672,4.93861e-09,-549.544) rot=(1,0,0;1.5708rad)
  ResizeMode = 0
FEATURE [PartDesign::ShapeBinder] CopyChamfer003
  Placement = pos=(0,4.93861e-09,-549.544) rot=(0,0,1;0rad)
  TraceSupport = false
FEATURE [PartDesign::Line] DatumLine003
  AttacherType = Attacher::AttachEngineLine
  AttachmentSupport = -> [CopyChamfer003]
  Length = 20
  MapMode = 29
  Placement = pos=(3.94672,4.93861e-09,-549.544) rot=(1,0,0;1.5708rad)
  ResizeMode = 0
FEATURE [PartDesign::ShapeBinder] CopyChamfer004
  Placement = pos=(0,4.93861e-09,-549.544) rot=(0,0,1;0rad)
  TraceSupport = false
FEATURE [PartDesign::Line] DatumLine004
  AttacherType = Attacher::AttachEngineLine
  AttachmentSupport = -> [CopyChamfer004]
  Length = 20
  MapMode = 19
  Placement = pos=(-1.554e-13,2.99207,-549.544) rot=(0,0,1;3.14159rad)
  ResizeMode = 0
FEATURE [PartDesign::ShapeBinder] CopyChamfer005
  Placement = pos=(0,4.93861e-09,-549.544) rot=(0,0,1;0rad)
  TraceSupport = false
FEATURE [PartDesign::Line] DatumLine005
  AttacherType = Attacher::AttachEngineLine
  AttachmentSupport = -> [CopyChamfer005]
  Length = 20
  MapMode = 19
  Placement = pos=(-1.55e-13,28.5871,-549.544) rot=(0,0,1;0rad)
  ResizeMode = 0
FEATURE [Sketcher::SketchObject] Sketch048
  ArcFitTolerance = 1e-06
  AttachmentSupport = -> [DatumPlane009]
  ExternalGeometry = -> [CopyChamfer001]
  FullyConstrained = false
  MakeInternals = false
  MapMode = 5
  Placement = pos=(-1.563e-13,15.7896,-564.544) rot=(0,0,1;1.5708rad)
  sketch-geometry (1):
    g0: Circle CenterX=0 CenterY=0 CenterZ=0 NormalX=0 NormalY=0 NormalZ=1 AngleXU=0 Radius=17.5
  constraints (1):
    c: Coincident(g0,g-1)
FEATURE [PartDesign::Pad] Pad032
  Direction = (0,-8.987e-12,1)
  Length = 10
  Length2 = 10
  Placement = pos=(-1.563e-13,15.7896,-564.544) rot=(0,0,1;1.5708rad)
  Profile = -> Sketch048
  ReferenceAxis = -> Sketch048 [N_Axis]
  Refine = true
  Suppressed = false
  Type = 0
FEATURE [Sketcher::SketchObject] Sketch049
  ArcFitTolerance = 1e-06
  AttachmentSupport = -> [Pad032]
  ExternalGeometry = -> [CopyChamfer004,CopyChamfer005]
  FullyConstrained = false
  MakeInternals = false
  MapMode = 5
  Placement = pos=(-1.563e-13,15.7896,-554.544) rot=(0,0,1;1.5708rad)
  sketch-geometry (4):
    g0: ArcOfCircle CenterX=-12.7975 CenterY=-1.315e-13 CenterZ=0 NormalX=0 NormalY=0 NormalZ=1 AngleXU=0 Radius=3.94672 StartAngle=1.5708 EndAngle=4.71239
    g1: ArcOfCircle CenterX=12.7975 CenterY=-1.315e-13 CenterZ=0 NormalX=0 NormalY=0 NormalZ=1 AngleXU=0 Radius=3.94672 StartAngle=4.71239 EndAngle=7.85398
    g2: LineSegment StartX=-12.7975 StartY=3.94672 StartZ=0 EndX=12.7975 EndY=3.94672 EndZ=0
    g3: LineSegment StartX=-12.7975 StartY=-3.94672 StartZ=0 EndX=12.7975 EndY=-3.94672 EndZ=0
  constraints (6):
    c: Tangent(g0,g2) = 1.5708
    c: Tangent(g0,g3) = -1.5708
    c: Tangent(g1,g2) = 1.5708
    c: Tangent(g1,g3) = -1.5708
    c: Equal(g0,g1)
    c: Horizontal(g3)
FEATURE [PartDesign::Pad] Pad033
  BaseFeature = -> Pad032
  Direction = (0,-8.9867e-12,1)
  Length = 5
  Length2 = 10
  Placement = pos=(-1.563e-13,15.7896,-564.544) rot=(0,0,1;1.5708rad)
  Profile = -> Sketch049
  ReferenceAxis = -> Sketch049 [N_Axis]
  Refine = true
  Suppressed = false
  Type = 0
FEATURE [PartDesign::Fillet] Fillet011
  Base = -> Pad033 [Edge3]
  BaseFeature = -> Pad033
  Placement = pos=(-1.563e-13,15.7896,-564.544) rot=(0,0,1;1.5708rad)
  Radius = 0.5
  Refine = true
  SupportTransform = false
  Suppressed = false
  UseAllEdges = false
FEATURE [PartDesign::Fillet] Fillet012
  Base = -> Fillet011 [Edge9]
  BaseFeature = -> Fillet011
  Placement = pos=(-1.563e-13,15.7896,-564.544) rot=(0,0,1;1.5708rad)
  Radius = 0.5
  Refine = true
  SupportTransform = false
  Suppressed = false
  UseAllEdges = false
FEATURE [PartDesign::Fillet] Fillet013
  Base = -> Fillet012 [Edge28]
  BaseFeature = -> Fillet012
  Placement = pos=(-1.563e-13,15.7896,-564.544) rot=(0,0,1;1.5708rad)
  Radius = 2
  Refine = true
  SupportTransform = false
  Suppressed = false
  UseAllEdges = false
FEATURE [PartDesign::Body] Body014
  AllowCompound = false
  Group = -> [DatumPlane009,CopyChamfer001,DatumLine002,CopyChamfer002,DatumLine003,CopyChamfer003,DatumLine004,CopyChamfer004,DatumLine005,CopyChamfer005,Sketch048,Pad032,Sketch049,Pad033,Fillet011,Fillet012,Fillet013]
  Origin = -> Origin009
  Tip = -> Fillet013
FEATURE [PartDesign::ShapeBinder] CopyChamfer006
  Placement = pos=(-1.55e-13,5.07345e-09,-564.544) rot=(0,0,1;0rad)
  TraceSupport = false
FEATURE [PartDesign::Plane] DatumPlane010
  AttachmentSupport = -> [CopyChamfer006]
  Length = 68.9291
  MapMode = 11
  Placement = pos=(32.7753,-26.9693,-564.544) rot=(0,0,1;1.5708rad)
  ResizeMode = 0
  Width = 74.7356
FEATURE [Sketcher::SketchObject] Sketch050
  ArcFitTolerance = 1e-06
  AttachmentSupport = -> [DatumPlane010]
  ExternalGeometry = -> [CopyChamfer006]
  FullyConstrained = false
  MakeInternals = false
  MapMode = 5
  Placement = pos=(32.7753,-26.9693,-564.544) rot=(0,0,1;1.5708rad)
  sketch-geometry (1):
    g0: Circle CenterX=0 CenterY=0 CenterZ=0 NormalX=0 NormalY=0 NormalZ=1 AngleXU=0 Radius=5
  constraints (1):
    c: Coincident(g0,g-1)
FEATURE [PartDesign::Pad] Pad034
  Direction = (0,-8.987e-12,1)
  Length = 10
  Length2 = 10
  Placement = pos=(32.7753,-26.9693,-564.544) rot=(0,0,1;1.5708rad)
  Profile = -> Sketch050
  ReferenceAxis = -> Sketch050 [N_Axis]
  Refine = true
  Suppressed = false
  Type = 0
FEATURE [PartDesign::Fillet] Fillet014
  Base = -> Pad034 [Edge3]
  BaseFeature = -> Pad034
  Placement = pos=(32.7753,-26.9693,-564.544) rot=(0,0,1;1.5708rad)
  Radius = 2
  Refine = true
  SupportTransform = false
  Suppressed = false
  UseAllEdges = false
FEATURE [PartDesign::Body] Body015
  AllowCompound = false
  Group = -> [DatumPlane010,CopyChamfer006,Sketch050,Pad034,Fillet014]
  Origin = -> Origin010
  Tip = -> Fillet014
FEATURE [PartDesign::ShapeBinder] CopyChamfer007
  Placement = pos=(-1.55e-13,5.07345e-09,-564.544) rot=(0,0,1;0rad)
  TraceSupport = false
FEATURE [PartDesign::Plane] DatumPlane011
  AttachmentSupport = -> [CopyChamfer007]
  Length = 67.6429
  MapMode = 11
  Placement = pos=(16.3876,-26.9693,-564.544) rot=(0,0,1;1.5708rad)
  ResizeMode = 0
  Width = 60.6742
FEATURE [Sketcher::SketchObject] Sketch051
  ArcFitTolerance = 1e-06
  AttachmentSupport = -> [DatumPlane011]
  ExternalGeometry = -> [CopyChamfer007]
  FullyConstrained = false
  MakeInternals = false
  MapMode = 5
  Placement = pos=(16.3876,-26.9693,-564.544) rot=(0,0,1;1.5708rad)
  sketch-geometry (1):
    g0: Circle CenterX=0 CenterY=0 CenterZ=0 NormalX=0 NormalY=0 NormalZ=1 AngleXU=0 Radius=5
  constraints (1):
    c: Coincident(g0,g-1)
FEATURE [PartDesign::Pad] Pad035
  Direction = (0,-8.987e-12,1)
  Length = 10
  Length2 = 10
  Placement = pos=(16.3876,-26.9693,-564.544) rot=(0,0,1;1.5708rad)
  Profile = -> Sketch051
  ReferenceAxis = -> Sketch051 [N_Axis]
  Refine = true
  Suppressed = false
  Type = 0
FEATURE [PartDesign::Fillet] Fillet015
  Base = -> Pad035 [Edge3]
  BaseFeature = -> Pad035
  Placement = pos=(16.3876,-26.9693,-564.544) rot=(0,0,1;1.5708rad)
  Radius = 2
  Refine = true
  SupportTransform = false
  Suppressed = false
  UseAllEdges = false
FEATURE [PartDesign::Body] Body016
  AllowCompound = false
  Group = -> [DatumPlane011,CopyChamfer007,Sketch051,Pad035,Fillet015]
  Origin = -> Origin012
  Tip = -> Fillet015
FEATURE [PartDesign::ShapeBinder] CopyChamfer008
  Placement = pos=(-1.55e-13,5.07345e-09,-564.544) rot=(0,0,1;0rad)
  TraceSupport = false
FEATURE [PartDesign::Plane] DatumPlane012
  AttachmentSupport = -> [CopyChamfer008]
  Length = 67.6429
  MapMode = 11
  Placement = pos=(-1.554e-13,-26.9693,-564.544) rot=(0,0,1;1.5708rad)
  ResizeMode = 0
  Width = 60.6742
FEATURE [Sketcher::SketchObject] Sketch052
  ArcFitTolerance = 1e-06
  AttachmentSupport = -> [DatumPlane012]
  ExternalGeometry = -> [CopyChamfer008]
  FullyConstrained = false
  MakeInternals = false
  MapMode = 5
  Placement = pos=(-1.554e-13,-26.9693,-564.544) rot=(0,0,1;1.5708rad)
  sketch-geometry (1):
    g0: Circle CenterX=0 CenterY=0 CenterZ=0 NormalX=0 NormalY=0 NormalZ=1 AngleXU=0 Radius=5
  constraints (1):
    c: Coincident(g0,g-1)
FEATURE [PartDesign::Pad] Pad036
  Direction = (0,-8.987e-12,1)
  Length = 10
  Length2 = 10
  Placement = pos=(-1.554e-13,-26.9693,-564.544) rot=(0,0,1;1.5708rad)
  Profile = -> Sketch052
  ReferenceAxis = -> Sketch052 [N_Axis]
  Refine = true
  Suppressed = false
  Type = 0
FEATURE [PartDesign::Fillet] Fillet016
  Base = -> Pad036 [Edge3]
  BaseFeature = -> Pad036
  Placement = pos=(-1.554e-13,-26.9693,-564.544) rot=(0,0,1;1.5708rad)
  Radius = 2
  Refine = true
  SupportTransform = false
  Suppressed = false
  UseAllEdges = false
FEATURE [PartDesign::Body] Body017
  AllowCompound = false
  Group = -> [DatumPlane012,CopyChamfer008,Sketch052,Pad036,Fillet016]
  Origin = -> Origin013
  Tip = -> Fillet016
FEATURE [PartDesign::ShapeBinder] CopyChamfer009
  Placement = pos=(-1.55e-13,5.07345e-09,-564.544) rot=(0,0,1;0rad)
  TraceSupport = false
FEATURE [PartDesign::Plane] DatumPlane013
  AttachmentSupport = -> [CopyChamfer009]
  Length = 67.6429
  MapMode = 11
  Placement = pos=(-16.3876,-26.9693,-564.544) rot=(0,0,1;1.5708rad)
  ResizeMode = 0
  Width = 60.6742
FEATURE [Sketcher::SketchObject] Sketch053
  ArcFitTolerance = 1e-06
  AttachmentSupport = -> [DatumPlane013]
  ExternalGeometry = -> [CopyChamfer009]
  FullyConstrained = false
  MakeInternals = false
  MapMode = 5
  Placement = pos=(-16.3876,-26.9693,-564.544) rot=(0,0,1;1.5708rad)
  sketch-geometry (1):
    g0: Circle CenterX=0 CenterY=0 CenterZ=0 NormalX=0 NormalY=0 NormalZ=1 AngleXU=0 Radius=5
  constraints (1):
    c: Coincident(g0,g-1)
FEATURE [PartDesign::Pad] Pad037
  Direction = (0,-8.987e-12,1)
  Length = 10
  Length2 = 10
  Placement = pos=(-16.3876,-26.9693,-564.544) rot=(0,0,1;1.5708rad)
  Profile = -> Sketch053
  ReferenceAxis = -> Sketch053 [N_Axis]
  Refine = true
  Suppressed = false
  Type = 0
FEATURE [PartDesign::Fillet] Fillet017
  Base = -> Pad037 [Edge3]
  BaseFeature = -> Pad037
  Placement = pos=(-16.3876,-26.9693,-564.544) rot=(0,0,1;1.5708rad)
  Radius = 2
  Refine = true
  SupportTransform = false
  Suppressed = false
  UseAllEdges = false
FEATURE [PartDesign::Body] Body018
  AllowCompound = false
  Group = -> [DatumPlane013,CopyChamfer009,Sketch053,Pad037,Fillet017]
  Origin = -> Origin014
  Tip = -> Fillet017
FEATURE [PartDesign::ShapeBinder] CopyChamfer010
  Placement = pos=(-1.55e-13,5.07345e-09,-564.544) rot=(0,0,1;0rad)
  TraceSupport = false
FEATURE [PartDesign::Plane] DatumPlane014
  AttachmentSupport = -> [CopyChamfer010]
  Length = 68.9291
  MapMode = 11
  Placement = pos=(-32.7753,-26.9693,-564.544) rot=(0,0,1;1.5708rad)
  ResizeMode = 0
  Width = 74.7351
FEATURE [Sketcher::SketchObject] Sketch054
  ArcFitTolerance = 1e-06
  AttachmentSupport = -> [DatumPlane014]
  ExternalGeometry = -> [CopyChamfer010]
  FullyConstrained = false
  MakeInternals = false
  MapMode = 5
  Placement = pos=(-32.7753,-26.9693,-564.544) rot=(0,0,1;1.5708rad)
  sketch-geometry (1):
    g0: Circle CenterX=0 CenterY=0 CenterZ=0 NormalX=0 NormalY=0 NormalZ=1 AngleXU=0 Radius=5
  constraints (1):
    c: Coincident(g0,g-1)
FEATURE [PartDesign::Pad] Pad038
  Direction = (0,-8.987e-12,1)
  Length = 10
  Length2 = 10
  Placement = pos=(-32.7753,-26.9693,-564.544) rot=(0,0,1;1.5708rad)
  Profile = -> Sketch054
  ReferenceAxis = -> Sketch054 [N_Axis]
  Refine = true
  Suppressed = false
  Type = 0
FEATURE [PartDesign::Fillet] Fillet018
  Base = -> Pad038 [Edge3]
  BaseFeature = -> Pad038
  Placement = pos=(-32.7753,-26.9693,-564.544) rot=(0,0,1;1.5708rad)
  Radius = 2
  Refine = true
  SupportTransform = false
  Suppressed = false
  UseAllEdges = false
FEATURE [PartDesign::Body] Body019
  AllowCompound = false
  Group = -> [DatumPlane014,CopyChamfer010,Sketch054,Pad038,Fillet018]
  Origin = -> Origin015
  Tip = -> Fillet018
FEATURE [App::Part] Part001  label="Buttons"
  Group = -> [Body015,Body016,Body017,Body018,Body019]
  Origin = -> Origin011
FEATURE [Sketcher::SketchObject] Sketch055
  ArcFitTolerance = 1e-06
  AttachmentSupport = -> [Chamfer001]
  ExternalGeometry = -> [Chamfer001]
  FullyConstrained = true
  MakeInternals = false
  MapMode = 5
  Placement = pos=(0,4.98354e-09,-554.544) rot=(0,0,1;0rad)
  sketch-geometry (5):
    g0: Circle CenterX=-32.7753 CenterY=-26.9693 CenterZ=0 NormalX=0 NormalY=0 NormalZ=1 AngleXU=0 Radius=5
    g1: Circle CenterX=-16.3876 CenterY=-26.9693 CenterZ=0 NormalX=0 NormalY=0 NormalZ=1 AngleXU=0 Radius=5
    g2: Circle CenterX=0 CenterY=-26.9693 CenterZ=0 NormalX=0 NormalY=0 NormalZ=1 AngleXU=0 Radius=5
    g3: Circle CenterX=16.3876 CenterY=-26.9693 CenterZ=0 NormalX=0 NormalY=0 NormalZ=1 AngleXU=0 Radius=5
    g4: Circle CenterX=32.7753 CenterY=-26.9693 CenterZ=0 NormalX=0 NormalY=0 NormalZ=1 AngleXU=0 Radius=5
  constraints (10):
    c: Coincident(g0,g-7)
    c: Equal(g0,g-7)
    c: Coincident(g1,g-6)
    c: Equal(g1,g-6)
    c: Coincident(g2,g-3)
    c: Equal(g2,g-3)
    c: Coincident(g3,g-4)
    c: Equal(g3,g-4)
    c: Coincident(g4,g-5)
    c: Equal(g4,g-5)
FEATURE [PartDesign::Pocket] Pocket007
  BaseFeature = -> Chamfer001
  Direction = (0,8.9866e-12,-1)
  Length = 10
  Length2 = 5
  Placement = pos=(0,2.33659e-09,-260) rot=(0,0,1;0rad)
  Profile = -> Sketch055
  ReferenceAxis = -> Sketch055 [N_Axis]
  Refine = true
  Suppressed = false
  Type = 0
FEATURE [Sketcher::SketchObject] Sketch056
  ArcFitTolerance = 1e-06
  AttachmentSupport = -> [Pocket007]
  ExternalGeometry = -> [Pocket007]
  FullyConstrained = true
  MakeInternals = false
  MapMode = 5
  Placement = pos=(0,4.93855e-09,-549.544) rot=(0,0,1;0rad)
  sketch-geometry (1):
    g0: Circle CenterX=0 CenterY=15.7896 CenterZ=0 NormalX=0 NormalY=0 NormalZ=1 AngleXU=0 Radius=17.5
  constraints (2):
    c: Coincident(g0,g-3)
    c: Equal(g0,g-3)
FEATURE [PartDesign::Pocket] Pocket008
  BaseFeature = -> Pocket007
  Direction = (0,8.9864e-12,-1)
  Length = 15
  Length2 = 5
  Placement = pos=(0,2.33659e-09,-260) rot=(0,0,1;0rad)
  Profile = -> Sketch056
  ReferenceAxis = -> Sketch056 [N_Axis]
  Refine = true
  Suppressed = false
  Type = 0
FEATURE [PartDesign::Body] Body005
  AllowCompound = false
  Group = -> [DatumPlane005,CopyPad020,CopyPad021,Sketch034,Pad021,Sketch035,Pad022,Fillet004,Sketch036,Pocket004,Sketch037,Pad023,Fillet005,Sketch038,Pad024,Fillet006,Fillet007,Fillet008,Chamfer001,Sketch055,Pocket007,Sketch056,Pocket008]
  Origin = -> Origin005
  Tip = -> Pocket008
FEATURE [Part::FeaturePython] Clone  label="body_part1"  # Draft clone (typed FeaturePython)
  AttacherType = Attacher::AttachEngine3D
  Fuse = false
  Objects = -> [Body003]
  Placement = pos=(0,0,599.54) rot=(0,0,1;0rad)
  Scale = (1,1,1)
FEATURE [App::Part] Part002  label="body_part1_p"
  Group = -> [Clone]
  Origin = -> Origin016
  Placement = pos=(0,0,599.54) rot=(0,0,1;0rad)
FEATURE [Part::FeaturePython] Clone001  label="body_part2"  # Draft clone (typed FeaturePython)
  AttacherType = Attacher::AttachEngine3D
  Fuse = false
  Objects = -> [Body004]
  Placement = pos=(0,0,599.54) rot=(0,0,1;0rad)
  Scale = (1,1,1)
FEATURE [App::Part] Part003  label="body_part2_p"
  Group = -> [Clone001]
  Origin = -> Origin017
  Placement = pos=(0,0,599.54) rot=(0,0,1;0rad)
FEATURE [Part::FeaturePython] Clone002  label="body_part3"  # Draft clone (typed FeaturePython)
  AttacherType = Attacher::AttachEngine3D
  Fuse = false
  Objects = -> [Body005]
  Placement = pos=(0,0,599.54) rot=(0,0,1;0rad)
  Scale = (1,1,1)
FEATURE [App::Part] Part004  label="body_part3_p"
  Group = -> [Clone002]
  Origin = -> Origin018
  Placement = pos=(0,0,599.54) rot=(0,0,1;0rad)
FEATURE [Part::FeaturePython] Clone003  label="fan_part1"  # Draft clone (typed FeaturePython)
  AttacherType = Attacher::AttachEngine3D
  Fuse = false
  Objects = -> [Body]
  Placement = pos=(0,0,599.54) rot=(0,0,1;0rad)
  Scale = (1,1,1)
FEATURE [App::Part] Part005  label="fan_part1_p"
  Group = -> [Clone003]
  Origin = -> Origin019
  Placement = pos=(0,0,599.54) rot=(0,0,1;0rad)
FEATURE [Part::FeaturePython] Clone004  label="fan_part2"  # Draft clone (typed FeaturePython)
  AttacherType = Attacher::AttachEngine3D
  Fuse = false
  Objects = -> [Body002]
  Placement = pos=(0,0,599.54) rot=(0,0,1;0rad)
  Scale = (1,1,1)
FEATURE [App::Part] Part006  label="fan_part2_p"
  Group = -> [Clone004]
  Origin = -> Origin020
  Placement = pos=(0,0,599.54) rot=(0,0,1;0rad)
FEATURE [Part::FeaturePython] Clone005  label="fan_part3"  # Draft clone (typed FeaturePython)
  AttacherType = Attacher::AttachEngine3D
  Fuse = false
  Objects = -> [Body001]
  Placement = pos=(0,0,599.54) rot=(0,0,1;0rad)
  Scale = (1,1,1)
FEATURE [App::Part] Part007  label="fan_part3_p"
  Group = -> [Clone005]
  Origin = -> Origin021
  Placement = pos=(0,0,599.54) rot=(0,0,1;0rad)
FEATURE [Part::FeaturePython] Clone006  label="fan_part4"  # Draft clone (typed FeaturePython)
  AttacherType = Attacher::AttachEngine3D
  Fuse = false
  Objects = -> [Body006]
  Placement = pos=(0,0,599.54) rot=(0,0,1;0rad)
  Scale = (1,1,1)
FEATURE [App::Part] Part008  label="fan_part4_p"
  Group = -> [Clone006]
  Origin = -> Origin022
  Placement = pos=(0,0,599.54) rot=(0,0,1;0rad)
FEATURE [Part::FeaturePython] Clone007  label="button_part1"  # Draft clone (typed FeaturePython)
  AttacherType = Attacher::AttachEngine3D
  Fuse = false
  Objects = -> [Body014]
  Placement = pos=(0,0,599.54) rot=(0,0,1;0rad)
  Scale = (1,1,1)
FEATURE [App::Part] Part009  label="button_part1_p"
  Group = -> [Clone007]
  Origin = -> Origin023
  Placement = pos=(0,0,599.54) rot=(0,0,1;0rad)
FEATURE [Part::FeaturePython] Clone008  label="button_part2"  # Draft clone (typed FeaturePython)
  AttacherType = Attacher::AttachEngine3D
  Fuse = false
  Objects = -> [Part001]
  Placement = pos=(0,0,599.54) rot=(0,0,1;0rad)
  Scale = (1,1,1)
FEATURE [App::Part] Part010  label="button_part2_p"
  Group = -> [Clone008]
  Origin = -> Origin024
  Placement = pos=(0,0,599.54) rot=(0,0,1;0rad)
FEATURE [Part::FeaturePython] Clone009  label="body_part1_clone"  # Draft clone (typed FeaturePython)
  AttacherType = Attacher::AttachEngine3D
  Fuse = false
  Objects = -> [Part002]
  Scale = (1,1,1)
FEATURE [Part::FeaturePython] Clone010  label="body_part2_clone"  # Draft clone (typed FeaturePython)
  AttacherType = Attacher::AttachEngine3D
  Fuse = false
  Objects = -> [Part003]
  Scale = (1,1,1)
FEATURE [Part::FeaturePython] Clone011  label="body_part3_clone"  # Draft clone (typed FeaturePython)
  AttacherType = Attacher::AttachEngine3D
  Fuse = false
  Objects = -> [Part004]
  Scale = (1,1,1)
FEATURE [Part::FeaturePython] Clone012  label="fan_part1_clone"  # Draft clone (typed FeaturePython)
  AttacherType = Attacher::AttachEngine3D
  Fuse = false
  Objects = -> [Part005]
  Scale = (1,1,1)
FEATURE [Part::FeaturePython] Clone013  label="fan_part2_clone"  # Draft clone (typed FeaturePython)
  AttacherType = Attacher::AttachEngine3D
  Fuse = false
  Objects = -> [Part006]
  Scale = (1,1,1)
FEATURE [Part::FeaturePython] Clone014  label="fan_part3_clone"  # Draft clone (typed FeaturePython)
  AttacherType = Attacher::AttachEngine3D
  Fuse = false
  Objects = -> [Part007]
  Scale = (1,1,1)
FEATURE [Part::FeaturePython] Clone015  label="fan_part4_clone"  # Draft clone (typed FeaturePython)
  AttacherType = Attacher::AttachEngine3D
  Fuse = false
  Objects = -> [Part008]
  Scale = (1,1,1)
FEATURE [Part::FeaturePython] Clone016  label="button_part1_clone"  # Draft clone (typed FeaturePython)
  AttacherType = Attacher::AttachEngine3D
  Fuse = false
  Objects = -> [Part009]
  Scale = (1,1,1)
FEATURE [Part::FeaturePython] Clone017  label="button_part2_clone"  # Draft clone (typed FeaturePython)
  AttacherType = Attacher::AttachEngine3D
  Fuse = false
  Objects = -> [Part010]
  Scale = (1,1,1)
FEATURE [App::Part] Part011  label="fan"
  Group = -> [Clone009,Clone010,Clone011,Clone012,Clone013,Clone014,Clone015,Clone016,Clone017]
  Origin = -> Origin025
